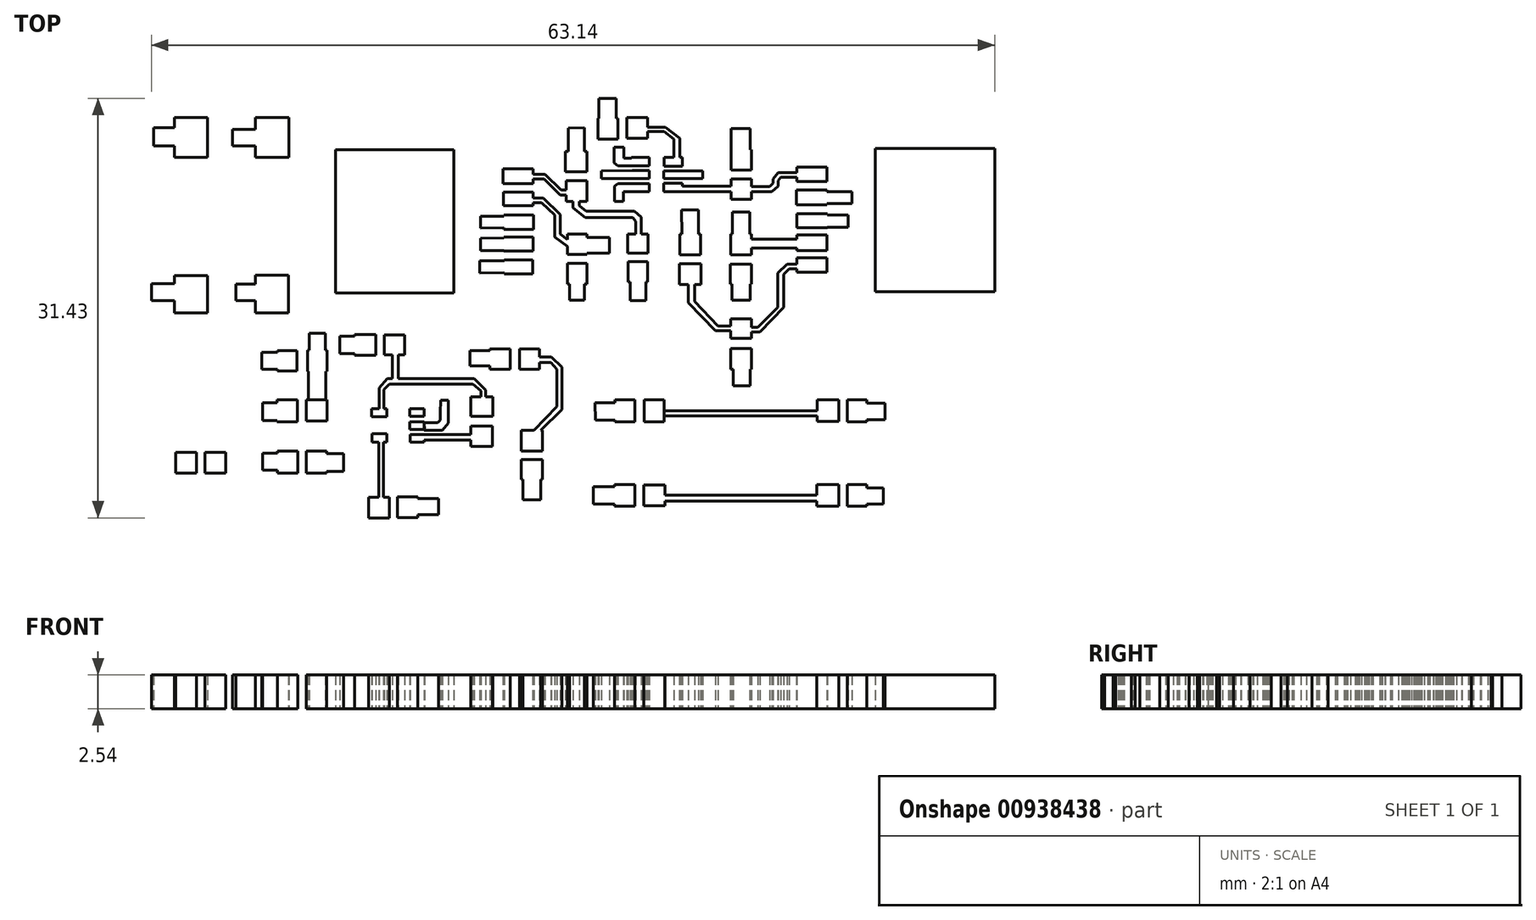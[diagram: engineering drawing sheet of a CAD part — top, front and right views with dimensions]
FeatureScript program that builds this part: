
annotation { "Feature Type Name" : "Feature", "Feature Type Description" : "" }
export const myFeature = defineFeature(function(context is Context, id is Id, definition is map)
    precondition{}
    {
        {
            var Q0;
            Q0=qCreatedBy(makeId("Top.planeOp"),FACE);
            var sketch = newSketch(context, id + "F0", { "sketchPlane" : qUnion([Q0])});
            skLineSegment(sketch, "E0.bottom", {"start": v(-32.78, 25.33) * mm, "end": v(35.8, 25.33) * mm});
            skLineSegment(sketch, "E0.top", {"start": v(-32.78, -28.01) * mm, "end": v(35.8, -28.01) * mm});
            skLineSegment(sketch, "E0.left", {"start": v(-32.78, 25.33) * mm, "end": v(-32.78, -28.01) * mm});
            skLineSegment(sketch, "E0.right", {"start": v(35.8, 25.33) * mm, "end": v(35.8, -28.01) * mm});
            skLineSegment(sketch, "E1.bottom", {"start": v(-28.35, 14.33) * mm, "end": v(-25.88, 14.33) * mm});
            skLineSegment(sketch, "E1.top", {"start": v(-28.35, 11.35) * mm, "end": v(-25.88, 11.35) * mm});
            skLineSegment(sketch, "E1.left", {"start": v(-28.35, 14.33) * mm, "end": v(-28.35, 11.35) * mm});
            skLineSegment(sketch, "E1.right", {"start": v(-25.88, 14.33) * mm, "end": v(-25.88, 11.35) * mm});
            skLineSegment(sketch, "E2.bottom", {"start": v(-22.29, 14.33) * mm, "end": v(-19.8, 14.33) * mm});
            skLineSegment(sketch, "E2.top", {"start": v(-22.29, 11.35) * mm, "end": v(-19.8, 11.35) * mm});
            skLineSegment(sketch, "E2.left", {"start": v(-22.29, 14.33) * mm, "end": v(-22.29, 11.35) * mm});
            skLineSegment(sketch, "E2.right", {"start": v(-19.8, 14.33) * mm, "end": v(-19.8, 11.35) * mm});
            skLineSegment(sketch, "E3.bottom", {"start": v(-28.35, 2.5) * mm, "end": v(-25.88, 2.5) * mm});
            skLineSegment(sketch, "E3.top", {"start": v(-28.35, -0.31) * mm, "end": v(-25.88, -0.31) * mm});
            skLineSegment(sketch, "E3.left", {"start": v(-28.35, 2.5) * mm, "end": v(-28.35, -0.31) * mm});
            skLineSegment(sketch, "E3.right", {"start": v(-25.88, 2.5) * mm, "end": v(-25.88, -0.31) * mm});
            skLineSegment(sketch, "E4.bottom", {"start": v(-22.29, 2.53) * mm, "end": v(-19.82, 2.53) * mm});
            skLineSegment(sketch, "E4.top", {"start": v(-22.29, -0.31) * mm, "end": v(-19.82, -0.31) * mm});
            skLineSegment(sketch, "E4.left", {"start": v(-22.29, 2.53) * mm, "end": v(-22.29, -0.31) * mm});
            skLineSegment(sketch, "E4.right", {"start": v(-19.82, 2.53) * mm, "end": v(-19.82, -0.31) * mm});
            skLineSegment(sketch, "E5.bottom", {"start": v(-28.24, -10.74) * mm, "end": v(-26.69, -10.74) * mm});
            skLineSegment(sketch, "E5.top", {"start": v(-28.24, -12.3) * mm, "end": v(-26.69, -12.3) * mm});
            skLineSegment(sketch, "E5.left", {"start": v(-28.24, -10.74) * mm, "end": v(-28.24, -12.3) * mm});
            skLineSegment(sketch, "E5.right", {"start": v(-26.69, -10.74) * mm, "end": v(-26.69, -12.3) * mm});
            skLineSegment(sketch, "E6.bottom", {"start": v(-26.08, -10.74) * mm, "end": v(-24.52, -10.74) * mm});
            skLineSegment(sketch, "E6.top", {"start": v(-26.08, -12.3) * mm, "end": v(-24.52, -12.3) * mm});
            skLineSegment(sketch, "E6.left", {"start": v(-26.08, -10.74) * mm, "end": v(-26.08, -12.3) * mm});
            skLineSegment(sketch, "E6.right", {"start": v(-24.52, -10.74) * mm, "end": v(-24.52, -12.3) * mm});
            skLineSegment(sketch, "E7.bottom", {"start": v(-20.64, -10.66) * mm, "end": v(-19.1, -10.66) * mm});
            skLineSegment(sketch, "E7.top", {"start": v(-20.64, -12.3) * mm, "end": v(-19.1, -12.3) * mm});
            skLineSegment(sketch, "E7.left", {"start": v(-20.64, -10.66) * mm, "end": v(-20.64, -12.3) * mm});
            skLineSegment(sketch, "E7.right", {"start": v(-19.1, -10.66) * mm, "end": v(-19.1, -12.3) * mm});
            skLineSegment(sketch, "E8.bottom", {"start": v(-18.47, -10.64) * mm, "end": v(-16.95, -10.64) * mm});
            skLineSegment(sketch, "E8.top", {"start": v(-18.47, -12.3) * mm, "end": v(-16.95, -12.3) * mm});
            skLineSegment(sketch, "E8.left", {"start": v(-18.47, -10.64) * mm, "end": v(-18.47, -12.3) * mm});
            skLineSegment(sketch, "E8.right", {"start": v(-16.95, -10.64) * mm, "end": v(-16.95, -12.3) * mm});
            skLineSegment(sketch, "E9.bottom", {"start": v(-20.66, -6.8) * mm, "end": v(-19.13, -6.8) * mm});
            skLineSegment(sketch, "E9.top", {"start": v(-20.66, -8.44) * mm, "end": v(-19.13, -8.44) * mm});
            skLineSegment(sketch, "E9.left", {"start": v(-20.66, -6.8) * mm, "end": v(-20.66, -8.44) * mm});
            skLineSegment(sketch, "E9.right", {"start": v(-19.13, -6.8) * mm, "end": v(-19.13, -8.44) * mm});
            skLineSegment(sketch, "E10.bottom", {"start": v(-18.47, -6.82) * mm, "end": v(-16.93, -6.82) * mm});
            skLineSegment(sketch, "E10.top", {"start": v(-18.47, -8.4) * mm, "end": v(-16.93, -8.4) * mm});
            skLineSegment(sketch, "E10.left", {"start": v(-18.47, -6.82) * mm, "end": v(-18.47, -8.4) * mm});
            skLineSegment(sketch, "E10.right", {"start": v(-16.93, -6.82) * mm, "end": v(-16.93, -8.4) * mm});
            skLineSegment(sketch, "E11.bottom", {"start": v(-20.64, -3.11) * mm, "end": v(-19.17, -3.11) * mm});
            skLineSegment(sketch, "E11.top", {"start": v(-20.64, -4.65) * mm, "end": v(-19.17, -4.65) * mm});
            skLineSegment(sketch, "E11.left", {"start": v(-20.64, -3.11) * mm, "end": v(-20.64, -4.65) * mm});
            skLineSegment(sketch, "E11.right", {"start": v(-19.17, -3.11) * mm, "end": v(-19.17, -4.65) * mm});
            skLineSegment(sketch, "E12.bottom", {"start": v(-18.38, -3.08) * mm, "end": v(-16.93, -3.08) * mm});
            skLineSegment(sketch, "E12.top", {"start": v(-18.38, -4.69) * mm, "end": v(-16.93, -4.69) * mm});
            skLineSegment(sketch, "E12.left", {"start": v(-18.38, -3.08) * mm, "end": v(-18.38, -4.69) * mm});
            skLineSegment(sketch, "E12.right", {"start": v(-16.93, -3.08) * mm, "end": v(-16.93, -4.69) * mm});
            skLineSegment(sketch, "E13.bottom", {"start": v(-14.86, -1.93) * mm, "end": v(-13.27, -1.93) * mm});
            skLineSegment(sketch, "E13.top", {"start": v(-14.86, -3.47) * mm, "end": v(-13.27, -3.47) * mm});
            skLineSegment(sketch, "E13.left", {"start": v(-14.86, -1.93) * mm, "end": v(-14.86, -3.47) * mm});
            skLineSegment(sketch, "E13.right", {"start": v(-13.27, -1.93) * mm, "end": v(-13.27, -3.47) * mm});
            skLineSegment(sketch, "E14.bottom", {"start": v(-12.63, -1.94) * mm, "end": v(-11.1, -1.94) * mm});
            skLineSegment(sketch, "E14.top", {"start": v(-12.63, -3.46) * mm, "end": v(-11.1, -3.46) * mm});
            skLineSegment(sketch, "E14.left", {"start": v(-12.63, -1.94) * mm, "end": v(-12.63, -3.46) * mm});
            skLineSegment(sketch, "E14.right", {"start": v(-11.1, -1.94) * mm, "end": v(-11.1, -3.46) * mm});
            skLineSegment(sketch, "E15.bottom", {"start": v(-13.59, -7.46) * mm, "end": v(-12.45, -7.46) * mm});
            skLineSegment(sketch, "E15.top", {"start": v(-13.59, -8.08) * mm, "end": v(-12.45, -8.08) * mm});
            skLineSegment(sketch, "E15.left", {"start": v(-13.59, -7.46) * mm, "end": v(-13.59, -8.08) * mm});
            skLineSegment(sketch, "E15.right", {"start": v(-12.45, -7.46) * mm, "end": v(-12.45, -8.08) * mm});
            skLineSegment(sketch, "E16.bottom", {"start": v(-10.74, -7.49) * mm, "end": v(-9.65, -7.49) * mm});
            skLineSegment(sketch, "E16.top", {"start": v(-10.74, -8.04) * mm, "end": v(-9.65, -8.04) * mm});
            skLineSegment(sketch, "E16.left", {"start": v(-10.74, -7.49) * mm, "end": v(-10.74, -8.04) * mm});
            skLineSegment(sketch, "E16.right", {"start": v(-9.65, -7.49) * mm, "end": v(-9.65, -8.04) * mm});
            skLineSegment(sketch, "E17.bottom", {"start": v(-10.74, -8.44) * mm, "end": v(-9.65, -8.44) * mm});
            skLineSegment(sketch, "E17.top", {"start": v(-10.74, -9.04) * mm, "end": v(-9.65, -9.04) * mm});
            skLineSegment(sketch, "E17.left", {"start": v(-10.74, -8.44) * mm, "end": v(-10.74, -9.04) * mm});
            skLineSegment(sketch, "E17.right", {"start": v(-9.65, -8.44) * mm, "end": v(-9.65, -9.04) * mm});
            skLineSegment(sketch, "E18.bottom", {"start": v(-10.69, -9.4) * mm, "end": v(-9.64, -9.4) * mm});
            skLineSegment(sketch, "E18.top", {"start": v(-10.69, -9.98) * mm, "end": v(-9.64, -9.98) * mm});
            skLineSegment(sketch, "E18.left", {"start": v(-10.69, -9.4) * mm, "end": v(-10.69, -9.98) * mm});
            skLineSegment(sketch, "E18.right", {"start": v(-9.64, -9.4) * mm, "end": v(-9.64, -9.98) * mm});
            skLineSegment(sketch, "E19.bottom", {"start": v(-13.56, -9.35) * mm, "end": v(-12.46, -9.35) * mm});
            skLineSegment(sketch, "E19.top", {"start": v(-13.56, -9.97) * mm, "end": v(-12.46, -9.97) * mm});
            skLineSegment(sketch, "E19.left", {"start": v(-13.56, -9.35) * mm, "end": v(-13.56, -9.97) * mm});
            skLineSegment(sketch, "E19.right", {"start": v(-12.46, -9.35) * mm, "end": v(-12.46, -9.97) * mm});
            skLineSegment(sketch, "E20.bottom", {"start": v(-6.15, -6.59) * mm, "end": v(-4.5, -6.59) * mm});
            skLineSegment(sketch, "E20.top", {"start": v(-6.15, -8.05) * mm, "end": v(-4.5, -8.05) * mm});
            skLineSegment(sketch, "E20.left", {"start": v(-6.15, -6.59) * mm, "end": v(-6.15, -8.05) * mm});
            skLineSegment(sketch, "E20.right", {"start": v(-4.5, -6.59) * mm, "end": v(-4.5, -8.05) * mm});
            skLineSegment(sketch, "E21.bottom", {"start": v(-6.15, -8.77) * mm, "end": v(-4.53, -8.77) * mm});
            skLineSegment(sketch, "E21.top", {"start": v(-6.15, -10.29) * mm, "end": v(-4.53, -10.29) * mm});
            skLineSegment(sketch, "E21.left", {"start": v(-6.15, -8.77) * mm, "end": v(-6.15, -10.29) * mm});
            skLineSegment(sketch, "E21.right", {"start": v(-4.53, -8.77) * mm, "end": v(-4.53, -10.29) * mm});
            skLineSegment(sketch, "E22.bottom", {"start": v(-13.82, -14.12) * mm, "end": v(-12.27, -14.12) * mm});
            skLineSegment(sketch, "E22.top", {"start": v(-13.82, -15.66) * mm, "end": v(-12.27, -15.66) * mm});
            skLineSegment(sketch, "E22.left", {"start": v(-13.82, -14.12) * mm, "end": v(-13.82, -15.66) * mm});
            skLineSegment(sketch, "E22.right", {"start": v(-12.27, -14.12) * mm, "end": v(-12.27, -15.66) * mm});
            skLineSegment(sketch, "E23.bottom", {"start": v(-11.64, -14.09) * mm, "end": v(-10.14, -14.09) * mm});
            skLineSegment(sketch, "E23.top", {"start": v(-11.64, -15.64) * mm, "end": v(-10.14, -15.64) * mm});
            skLineSegment(sketch, "E23.left", {"start": v(-11.64, -14.09) * mm, "end": v(-11.64, -15.64) * mm});
            skLineSegment(sketch, "E23.right", {"start": v(-10.14, -14.09) * mm, "end": v(-10.14, -15.64) * mm});
            skLineSegment(sketch, "E24.bottom", {"start": v(-2.38, -9.1) * mm, "end": v(-0.8, -9.1) * mm});
            skLineSegment(sketch, "E24.top", {"start": v(-2.38, -10.66) * mm, "end": v(-0.8, -10.66) * mm});
            skLineSegment(sketch, "E24.left", {"start": v(-2.38, -9.1) * mm, "end": v(-2.38, -10.66) * mm});
            skLineSegment(sketch, "E24.right", {"start": v(-0.8, -9.1) * mm, "end": v(-0.8, -10.66) * mm});
            skLineSegment(sketch, "E25.bottom", {"start": v(-2.4, -11.29) * mm, "end": v(-0.8, -11.29) * mm});
            skLineSegment(sketch, "E25.top", {"start": v(-2.4, -12.79) * mm, "end": v(-0.8, -12.79) * mm});
            skLineSegment(sketch, "E25.left", {"start": v(-2.4, -11.29) * mm, "end": v(-2.4, -12.79) * mm});
            skLineSegment(sketch, "E25.right", {"start": v(-0.8, -11.29) * mm, "end": v(-0.8, -12.79) * mm});
            skLineSegment(sketch, "E26.bottom", {"start": v(-4.75, -2.99) * mm, "end": v(-3.2, -2.99) * mm});
            skLineSegment(sketch, "E26.top", {"start": v(-4.75, -4.5) * mm, "end": v(-3.2, -4.5) * mm});
            skLineSegment(sketch, "E26.left", {"start": v(-4.75, -2.99) * mm, "end": v(-4.75, -4.5) * mm});
            skLineSegment(sketch, "E26.right", {"start": v(-3.2, -2.99) * mm, "end": v(-3.2, -4.5) * mm});
            skLineSegment(sketch, "E27.bottom", {"start": v(-2.5, -2.99) * mm, "end": v(-1.01, -2.99) * mm});
            skLineSegment(sketch, "E27.top", {"start": v(-2.5, -4.53) * mm, "end": v(-1.01, -4.53) * mm});
            skLineSegment(sketch, "E27.left", {"start": v(-2.5, -2.99) * mm, "end": v(-2.5, -4.53) * mm});
            skLineSegment(sketch, "E27.right", {"start": v(-1.01, -2.99) * mm, "end": v(-1.01, -4.53) * mm});
            skLineSegment(sketch, "E28.bottom", {"start": v(4.64, -6.82) * mm, "end": v(6.14, -6.82) * mm});
            skLineSegment(sketch, "E28.top", {"start": v(4.64, -8.45) * mm, "end": v(6.14, -8.45) * mm});
            skLineSegment(sketch, "E28.left", {"start": v(4.64, -6.82) * mm, "end": v(4.64, -8.45) * mm});
            skLineSegment(sketch, "E28.right", {"start": v(6.14, -6.82) * mm, "end": v(6.14, -8.45) * mm});
            skLineSegment(sketch, "E29.bottom", {"start": v(6.83, -6.82) * mm, "end": v(8.33, -6.82) * mm});
            skLineSegment(sketch, "E29.top", {"start": v(6.83, -8.46) * mm, "end": v(8.33, -8.46) * mm});
            skLineSegment(sketch, "E29.left", {"start": v(6.83, -6.82) * mm, "end": v(6.83, -8.46) * mm});
            skLineSegment(sketch, "E29.right", {"start": v(8.33, -6.82) * mm, "end": v(8.33, -8.46) * mm});
            skLineSegment(sketch, "E30.bottom", {"start": v(4.59, -13.14) * mm, "end": v(6.13, -13.14) * mm});
            skLineSegment(sketch, "E30.top", {"start": v(4.59, -14.79) * mm, "end": v(6.13, -14.79) * mm});
            skLineSegment(sketch, "E30.left", {"start": v(4.59, -13.14) * mm, "end": v(4.59, -14.79) * mm});
            skLineSegment(sketch, "E30.right", {"start": v(6.13, -13.14) * mm, "end": v(6.13, -14.79) * mm});
            skLineSegment(sketch, "E31.bottom", {"start": v(6.78, -13.18) * mm, "end": v(8.37, -13.18) * mm});
            skLineSegment(sketch, "E31.top", {"start": v(6.78, -14.75) * mm, "end": v(8.37, -14.75) * mm});
            skLineSegment(sketch, "E31.left", {"start": v(6.78, -13.18) * mm, "end": v(6.78, -14.75) * mm});
            skLineSegment(sketch, "E31.right", {"start": v(8.37, -13.18) * mm, "end": v(8.37, -14.75) * mm});
            skLineSegment(sketch, "E32.bottom", {"start": v(19.76, -13.17) * mm, "end": v(21.4, -13.17) * mm});
            skLineSegment(sketch, "E32.top", {"start": v(19.76, -14.77) * mm, "end": v(21.4, -14.77) * mm});
            skLineSegment(sketch, "E32.left", {"start": v(19.76, -13.17) * mm, "end": v(19.76, -14.77) * mm});
            skLineSegment(sketch, "E32.right", {"start": v(21.4, -13.17) * mm, "end": v(21.4, -14.77) * mm});
            skLineSegment(sketch, "E33.bottom", {"start": v(22.02, -13.15) * mm, "end": v(23.49, -13.15) * mm});
            skLineSegment(sketch, "E33.top", {"start": v(22.02, -14.77) * mm, "end": v(23.49, -14.77) * mm});
            skLineSegment(sketch, "E33.left", {"start": v(22.02, -13.15) * mm, "end": v(22.02, -14.77) * mm});
            skLineSegment(sketch, "E33.right", {"start": v(23.49, -13.15) * mm, "end": v(23.49, -14.77) * mm});
            skLineSegment(sketch, "E34.bottom", {"start": v(19.78, -6.82) * mm, "end": v(21.39, -6.82) * mm});
            skLineSegment(sketch, "E34.top", {"start": v(19.78, -8.44) * mm, "end": v(21.39, -8.44) * mm});
            skLineSegment(sketch, "E34.left", {"start": v(19.78, -6.82) * mm, "end": v(19.78, -8.44) * mm});
            skLineSegment(sketch, "E34.right", {"start": v(21.39, -6.82) * mm, "end": v(21.39, -8.44) * mm});
            skLineSegment(sketch, "E35.bottom", {"start": v(22.04, -6.82) * mm, "end": v(23.49, -6.82) * mm});
            skLineSegment(sketch, "E35.top", {"start": v(22.04, -8.47) * mm, "end": v(23.49, -8.47) * mm});
            skLineSegment(sketch, "E35.left", {"start": v(22.04, -6.82) * mm, "end": v(22.04, -8.47) * mm});
            skLineSegment(sketch, "E35.right", {"start": v(23.49, -6.82) * mm, "end": v(23.49, -8.47) * mm});
            skLineSegment(sketch, "E36.bottom", {"start": v(13.3, -0.74) * mm, "end": v(14.85, -0.74) * mm});
            skLineSegment(sketch, "E36.top", {"start": v(13.3, -2.22) * mm, "end": v(14.85, -2.22) * mm});
            skLineSegment(sketch, "E36.left", {"start": v(13.3, -0.74) * mm, "end": v(13.3, -2.22) * mm});
            skLineSegment(sketch, "E36.right", {"start": v(14.85, -0.74) * mm, "end": v(14.85, -2.22) * mm});
            skLineSegment(sketch, "E37.bottom", {"start": v(13.3, -2.96) * mm, "end": v(14.85, -2.96) * mm});
            skLineSegment(sketch, "E37.top", {"start": v(13.3, -4.53) * mm, "end": v(14.85, -4.53) * mm});
            skLineSegment(sketch, "E37.left", {"start": v(13.3, -2.96) * mm, "end": v(13.3, -4.53) * mm});
            skLineSegment(sketch, "E37.right", {"start": v(14.85, -2.96) * mm, "end": v(14.85, -4.53) * mm});
            skLineSegment(sketch, "E38.bottom", {"start": v(-16.28, 11.92) * mm, "end": v(-7.44, 11.92) * mm});
            skLineSegment(sketch, "E38.top", {"start": v(-16.28, 1.2) * mm, "end": v(-7.44, 1.2) * mm});
            skLineSegment(sketch, "E38.left", {"start": v(-16.28, 11.92) * mm, "end": v(-16.28, 1.2) * mm});
            skLineSegment(sketch, "E38.right", {"start": v(-7.44, 11.92) * mm, "end": v(-7.44, 1.2) * mm});
            skLineSegment(sketch, "E39.bottom", {"start": v(-3.76, 10.49) * mm, "end": v(-1.5, 10.49) * mm});
            skLineSegment(sketch, "E39.top", {"start": v(-3.76, 9.38) * mm, "end": v(-1.5, 9.38) * mm});
            skLineSegment(sketch, "E39.left", {"start": v(-3.76, 10.49) * mm, "end": v(-3.76, 9.38) * mm});
            skLineSegment(sketch, "E39.right", {"start": v(-1.5, 10.49) * mm, "end": v(-1.5, 9.38) * mm});
            skLineSegment(sketch, "E40.bottom", {"start": v(-3.7, 8.76) * mm, "end": v(-1.5, 8.76) * mm});
            skLineSegment(sketch, "E40.top", {"start": v(-3.7, 7.73) * mm, "end": v(-1.5, 7.73) * mm});
            skLineSegment(sketch, "E40.left", {"start": v(-3.7, 8.76) * mm, "end": v(-3.7, 7.73) * mm});
            skLineSegment(sketch, "E41.bottom", {"start": v(-3.67, 7.04) * mm, "end": v(-1.48, 7.04) * mm});
            skLineSegment(sketch, "E41.top", {"start": v(-3.67, 5.97) * mm, "end": v(-1.48, 5.97) * mm});
            skLineSegment(sketch, "E41.left", {"start": v(-3.67, 7.04) * mm, "end": v(-3.67, 5.97) * mm});
            skLineSegment(sketch, "E41.right", {"start": v(-1.48, 7.04) * mm, "end": v(-1.48, 5.97) * mm});
            skLineSegment(sketch, "E42.bottom", {"start": v(-3.67, 5.37) * mm, "end": v(-1.5, 5.37) * mm});
            skLineSegment(sketch, "E42.top", {"start": v(-3.67, 4.32) * mm, "end": v(-1.5, 4.32) * mm});
            skLineSegment(sketch, "E42.left", {"start": v(-3.67, 5.37) * mm, "end": v(-3.67, 4.32) * mm});
            skLineSegment(sketch, "E42.right", {"start": v(-1.5, 5.37) * mm, "end": v(-1.5, 4.32) * mm});
            skLineSegment(sketch, "E43.bottom", {"start": v(-3.66, 3.66) * mm, "end": v(-1.52, 3.66) * mm});
            skLineSegment(sketch, "E43.top", {"start": v(-3.66, 2.64) * mm, "end": v(-1.52, 2.64) * mm});
            skLineSegment(sketch, "E43.left", {"start": v(-3.66, 3.66) * mm, "end": v(-3.66, 2.64) * mm});
            skLineSegment(sketch, "E43.right", {"start": v(-1.52, 3.66) * mm, "end": v(-1.52, 2.64) * mm});
            skLineSegment(sketch, "E44.bottom", {"start": v(1.06, 5.6) * mm, "end": v(2.54, 5.6) * mm});
            skLineSegment(sketch, "E44.top", {"start": v(1.06, 4.1) * mm, "end": v(2.54, 4.1) * mm});
            skLineSegment(sketch, "E45.bottom", {"start": v(1.06, 3.4) * mm, "end": v(2.54, 3.4) * mm});
            skLineSegment(sketch, "E45.top", {"start": v(1.06, 1.85) * mm, "end": v(2.54, 1.85) * mm});
            skLineSegment(sketch, "E45.left", {"start": v(1.06, 3.4) * mm, "end": v(1.06, 1.85) * mm});
            skLineSegment(sketch, "E45.right", {"start": v(2.54, 3.4) * mm, "end": v(2.54, 1.85) * mm});
            skLineSegment(sketch, "E46.bottom", {"start": v(5.59, 5.6) * mm, "end": v(7.11, 5.6) * mm});
            skLineSegment(sketch, "E46.top", {"start": v(5.59, 4.2) * mm, "end": v(7.11, 4.2) * mm});
            skLineSegment(sketch, "E46.left", {"start": v(5.59, 5.6) * mm, "end": v(5.59, 4.2) * mm});
            skLineSegment(sketch, "E46.right", {"start": v(7.11, 5.6) * mm, "end": v(7.11, 4.2) * mm});
            skLineSegment(sketch, "E47.bottom", {"start": v(5.61, 3.54) * mm, "end": v(7.08, 3.54) * mm});
            skLineSegment(sketch, "E47.top", {"start": v(5.61, 2.01) * mm, "end": v(7.08, 2.01) * mm});
            skLineSegment(sketch, "E47.left", {"start": v(5.61, 3.54) * mm, "end": v(5.61, 2.01) * mm});
            skLineSegment(sketch, "E47.right", {"start": v(7.08, 3.54) * mm, "end": v(7.08, 2.01) * mm});
            skLineSegment(sketch, "E48.bottom", {"start": v(9.48, 5.6) * mm, "end": v(11.04, 5.6) * mm});
            skLineSegment(sketch, "E48.top", {"start": v(9.48, 4.05) * mm, "end": v(11.04, 4.05) * mm});
            skLineSegment(sketch, "E48.left", {"start": v(9.48, 5.6) * mm, "end": v(9.48, 4.05) * mm});
            skLineSegment(sketch, "E48.right", {"start": v(11.04, 5.6) * mm, "end": v(11.04, 4.05) * mm});
            skLineSegment(sketch, "E49.bottom", {"start": v(9.47, 3.38) * mm, "end": v(11.08, 3.38) * mm});
            skLineSegment(sketch, "E49.top", {"start": v(9.47, 1.84) * mm, "end": v(11.08, 1.84) * mm});
            skLineSegment(sketch, "E49.left", {"start": v(9.47, 3.38) * mm, "end": v(9.47, 1.84) * mm});
            skLineSegment(sketch, "E49.right", {"start": v(11.08, 3.38) * mm, "end": v(11.08, 1.84) * mm});
            skLineSegment(sketch, "E50.bottom", {"start": v(13.3, 5.6) * mm, "end": v(14.85, 5.6) * mm});
            skLineSegment(sketch, "E50.top", {"start": v(13.3, 4.05) * mm, "end": v(14.85, 4.05) * mm});
            skLineSegment(sketch, "E50.left", {"start": v(13.3, 5.6) * mm, "end": v(13.3, 4.05) * mm});
            skLineSegment(sketch, "E50.right", {"start": v(14.85, 5.6) * mm, "end": v(14.85, 4.05) * mm});
            skLineSegment(sketch, "E51.bottom", {"start": v(13.28, 3.36) * mm, "end": v(14.85, 3.36) * mm});
            skLineSegment(sketch, "E51.top", {"start": v(13.28, 1.87) * mm, "end": v(14.85, 1.87) * mm});
            skLineSegment(sketch, "E51.left", {"start": v(13.28, 3.36) * mm, "end": v(13.28, 1.87) * mm});
            skLineSegment(sketch, "E51.right", {"start": v(14.85, 3.36) * mm, "end": v(14.85, 1.87) * mm});
            skLineSegment(sketch, "E52.bottom", {"start": v(0.92, 11.8) * mm, "end": v(2.54, 11.8) * mm});
            skLineSegment(sketch, "E52.top", {"start": v(0.92, 10.26) * mm, "end": v(2.54, 10.26) * mm});
            skLineSegment(sketch, "E52.left", {"start": v(0.92, 11.8) * mm, "end": v(0.92, 10.26) * mm});
            skLineSegment(sketch, "E52.right", {"start": v(2.54, 11.8) * mm, "end": v(2.54, 10.26) * mm});
            skLineSegment(sketch, "E53.bottom", {"start": v(0.97, 9.62) * mm, "end": v(2.54, 9.62) * mm});
            skLineSegment(sketch, "E53.top", {"start": v(0.97, 8.05) * mm, "end": v(2.54, 8.05) * mm});
            skLineSegment(sketch, "E53.left", {"start": v(0.97, 9.62) * mm, "end": v(0.97, 8.05) * mm});
            skLineSegment(sketch, "E53.right", {"start": v(2.54, 9.62) * mm, "end": v(2.54, 8.05) * mm});
            skLineSegment(sketch, "E54.bottom", {"start": v(3.36, 14.27) * mm, "end": v(4.84, 14.27) * mm});
            skLineSegment(sketch, "E54.top", {"start": v(3.36, 12.73) * mm, "end": v(4.84, 12.73) * mm});
            skLineSegment(sketch, "E54.left", {"start": v(3.36, 14.27) * mm, "end": v(3.36, 12.73) * mm});
            skLineSegment(sketch, "E54.right", {"start": v(4.84, 14.27) * mm, "end": v(4.84, 12.73) * mm});
            skLineSegment(sketch, "E55.bottom", {"start": v(5.54, 14.33) * mm, "end": v(7.08, 14.33) * mm});
            skLineSegment(sketch, "E55.top", {"start": v(5.54, 12.77) * mm, "end": v(7.08, 12.77) * mm});
            skLineSegment(sketch, "E55.left", {"start": v(5.54, 14.33) * mm, "end": v(5.54, 12.77) * mm});
            skLineSegment(sketch, "E55.right", {"start": v(7.08, 14.33) * mm, "end": v(7.08, 12.77) * mm});
            skLineSegment(sketch, "E56.bottom", {"start": v(5.86, 11.35) * mm, "end": v(7.2, 11.35) * mm});
            skLineSegment(sketch, "E56.top", {"start": v(5.86, 10.72) * mm, "end": v(7.2, 10.72) * mm});
            skLineSegment(sketch, "E56.left", {"start": v(5.86, 11.35) * mm, "end": v(5.86, 10.72) * mm});
            skLineSegment(sketch, "E56.right", {"start": v(7.2, 11.35) * mm, "end": v(7.2, 10.72) * mm});
            skLineSegment(sketch, "E57.bottom", {"start": v(5.93, 10.35) * mm, "end": v(7.21, 10.35) * mm});
            skLineSegment(sketch, "E57.top", {"start": v(5.93, 9.76) * mm, "end": v(7.21, 9.76) * mm});
            skLineSegment(sketch, "E57.left", {"start": v(5.93, 10.35) * mm, "end": v(5.93, 9.76) * mm});
            skLineSegment(sketch, "E57.right", {"start": v(7.21, 10.35) * mm, "end": v(7.21, 9.76) * mm});
            skLineSegment(sketch, "E58.bottom", {"start": v(5.85, 9.4) * mm, "end": v(7.21, 9.4) * mm});
            skLineSegment(sketch, "E58.top", {"start": v(5.85, 8.78) * mm, "end": v(7.21, 8.78) * mm});
            skLineSegment(sketch, "E58.left", {"start": v(5.85, 9.4) * mm, "end": v(5.85, 8.78) * mm});
            skLineSegment(sketch, "E58.right", {"start": v(7.21, 9.4) * mm, "end": v(7.21, 8.78) * mm});
            skLineSegment(sketch, "E59.bottom", {"start": v(8.33, 11.35) * mm, "end": v(9.68, 11.35) * mm});
            skLineSegment(sketch, "E59.top", {"start": v(8.33, 10.67) * mm, "end": v(9.68, 10.67) * mm});
            skLineSegment(sketch, "E59.left", {"start": v(8.33, 11.35) * mm, "end": v(8.33, 10.67) * mm});
            skLineSegment(sketch, "E59.right", {"start": v(9.68, 11.35) * mm, "end": v(9.68, 10.67) * mm});
            skLineSegment(sketch, "E60.bottom", {"start": v(8.29, 10.34) * mm, "end": v(9.7, 10.34) * mm});
            skLineSegment(sketch, "E60.top", {"start": v(8.29, 9.77) * mm, "end": v(9.7, 9.77) * mm});
            skLineSegment(sketch, "E60.left", {"start": v(8.29, 10.34) * mm, "end": v(8.29, 9.77) * mm});
            skLineSegment(sketch, "E60.right", {"start": v(9.7, 10.34) * mm, "end": v(9.7, 9.77) * mm});
            skLineSegment(sketch, "E61.bottom", {"start": v(8.29, 9.42) * mm, "end": v(9.67, 9.42) * mm});
            skLineSegment(sketch, "E61.top", {"start": v(8.29, 8.78) * mm, "end": v(9.67, 8.78) * mm});
            skLineSegment(sketch, "E61.left", {"start": v(8.29, 9.42) * mm, "end": v(8.29, 8.78) * mm});
            skLineSegment(sketch, "E61.right", {"start": v(9.67, 9.42) * mm, "end": v(9.67, 8.78) * mm});
            skLineSegment(sketch, "E62.bottom", {"start": v(13.33, 11.94) * mm, "end": v(14.86, 11.94) * mm});
            skLineSegment(sketch, "E62.top", {"start": v(13.33, 10.4) * mm, "end": v(14.86, 10.4) * mm});
            skLineSegment(sketch, "E62.left", {"start": v(13.33, 11.94) * mm, "end": v(13.33, 10.4) * mm});
            skLineSegment(sketch, "E62.right", {"start": v(14.86, 11.94) * mm, "end": v(14.86, 10.4) * mm});
            skLineSegment(sketch, "E63.bottom", {"start": v(13.33, 9.73) * mm, "end": v(14.86, 9.73) * mm});
            skLineSegment(sketch, "E63.top", {"start": v(13.33, 8.2) * mm, "end": v(14.86, 8.2) * mm});
            skLineSegment(sketch, "E63.left", {"start": v(13.33, 9.73) * mm, "end": v(13.33, 8.2) * mm});
            skLineSegment(sketch, "E63.right", {"start": v(14.86, 9.73) * mm, "end": v(14.86, 8.2) * mm});
            skLineSegment(sketch, "E64.bottom", {"start": v(18.27, 10.62) * mm, "end": v(20.51, 10.62) * mm});
            skLineSegment(sketch, "E64.top", {"start": v(18.27, 9.55) * mm, "end": v(20.51, 9.55) * mm});
            skLineSegment(sketch, "E64.left", {"start": v(18.27, 10.62) * mm, "end": v(18.27, 9.55) * mm});
            skLineSegment(sketch, "E64.right", {"start": v(20.51, 10.62) * mm, "end": v(20.51, 9.55) * mm});
            skLineSegment(sketch, "E65.bottom", {"start": v(18.22, 8.91) * mm, "end": v(20.51, 8.91) * mm});
            skLineSegment(sketch, "E65.top", {"start": v(18.22, 7.81) * mm, "end": v(20.51, 7.81) * mm});
            skLineSegment(sketch, "E65.left", {"start": v(18.22, 8.91) * mm, "end": v(18.22, 7.81) * mm});
            skLineSegment(sketch, "E65.right", {"start": v(20.51, 8.91) * mm, "end": v(20.51, 7.81) * mm});
            skLineSegment(sketch, "E66.bottom", {"start": v(18.27, 7.13) * mm, "end": v(20.55, 7.13) * mm});
            skLineSegment(sketch, "E66.top", {"start": v(18.27, 6.07) * mm, "end": v(20.55, 6.07) * mm});
            skLineSegment(sketch, "E66.left", {"start": v(18.27, 7.13) * mm, "end": v(18.27, 6.07) * mm});
            skLineSegment(sketch, "E66.right", {"start": v(20.55, 7.13) * mm, "end": v(20.55, 6.07) * mm});
            skLineSegment(sketch, "E67.bottom", {"start": v(18.26, 5.56) * mm, "end": v(20.5, 5.56) * mm});
            skLineSegment(sketch, "E67.top", {"start": v(18.26, 4.38) * mm, "end": v(20.5, 4.38) * mm});
            skLineSegment(sketch, "E67.left", {"start": v(18.26, 5.56) * mm, "end": v(18.26, 4.38) * mm});
            skLineSegment(sketch, "E67.right", {"start": v(20.5, 5.56) * mm, "end": v(20.5, 4.38) * mm});
            skLineSegment(sketch, "E68.bottom", {"start": v(18.24, 3.83) * mm, "end": v(20.5, 3.83) * mm});
            skLineSegment(sketch, "E68.top", {"start": v(18.24, 2.76) * mm, "end": v(20.5, 2.76) * mm});
            skLineSegment(sketch, "E68.left", {"start": v(18.24, 3.83) * mm, "end": v(18.24, 2.76) * mm});
            skLineSegment(sketch, "E68.right", {"start": v(20.5, 3.83) * mm, "end": v(20.5, 2.76) * mm});
            skLineSegment(sketch, "E69.bottom", {"start": v(24.12, 12.03) * mm, "end": v(33.07, 12.03) * mm});
            skLineSegment(sketch, "E69.top", {"start": v(24.12, 1.3) * mm, "end": v(33.07, 1.3) * mm});
            skLineSegment(sketch, "E69.left", {"start": v(24.12, 12.03) * mm, "end": v(24.12, 1.3) * mm});
            skLineSegment(sketch, "E69.right", {"start": v(33.07, 12.03) * mm, "end": v(33.07, 1.3) * mm});
            skPoint(sketch, "E70.centerSnap0", {"position": v(-18.38, -3.89) * mm});
            skPoint(sketch, "E71.centerSnap0", {"position": v(-10.2, -7.49) * mm});
            skPoint(sketch, "E72.centerSnap0", {"position": v(14.06, 1.87) * mm});
            skLineSegment(sketch, "E73", {"start": v(-13.04, -14.12) * mm, "end": v(-13.04, -9.97) * mm});
            skLineSegment(sketch, "E74", {"start": v(-13.04, -9.97) * mm, "end": v(-12.7, -9.97) * mm});
            skLineSegment(sketch, "E75", {"start": v(-12.7, -9.97) * mm, "end": v(-12.7, -14.12) * mm});
            skLineSegment(sketch, "E76", {"start": v(-12.7, -14.12) * mm, "end": v(-13.04, -14.12) * mm});
            skLineSegment(sketch, "E77", {"start": v(-13.02, -7.46) * mm, "end": v(-13.02, -5.93) * mm});
            skLineSegment(sketch, "E78", {"start": v(-13.02, -5.93) * mm, "end": v(-12.43, -5.22) * mm});
            skLineSegment(sketch, "E79", {"start": v(-12.43, -5.22) * mm, "end": v(-12.05, -5.22) * mm});
            skLineSegment(sketch, "E80", {"start": v(-12.05, -5.22) * mm, "end": v(-12.05, -3.46) * mm});
            skLineSegment(sketch, "E81", {"start": v(-12.05, -3.46) * mm, "end": v(-11.6, -3.46) * mm});
            skLineSegment(sketch, "E82", {"start": v(-11.6, -3.46) * mm, "end": v(-11.6, -5.2) * mm});
            skLineSegment(sketch, "E83", {"start": v(-11.6, -5.2) * mm, "end": v(-5.9, -5.2) * mm});
            skLineSegment(sketch, "E84", {"start": v(-5.9, -5.2) * mm, "end": v(-5.05, -6.09) * mm});
            skLineSegment(sketch, "E85", {"start": v(-5.05, -6.09) * mm, "end": v(-5.05, -6.59) * mm});
            skLineSegment(sketch, "E86", {"start": v(-5.05, -6.59) * mm, "end": v(-5.33, -6.59) * mm});
            skLineSegment(sketch, "E87", {"start": v(-5.41, -6.59) * mm, "end": v(-5.41, -6.15) * mm});
            skLineSegment(sketch, "E88", {"start": v(-5.41, -6.15) * mm, "end": v(-6, -5.62) * mm});
            skLineSegment(sketch, "E89", {"start": v(-6, -5.62) * mm, "end": v(-12.26, -5.62) * mm});
            skLineSegment(sketch, "E90", {"start": v(-12.26, -5.62) * mm, "end": v(-12.66, -6.06) * mm});
            skLineSegment(sketch, "E91", {"start": v(-12.66, -6.06) * mm, "end": v(-12.66, -7.46) * mm});
            skLineSegment(sketch, "E92", {"start": v(-12.66, -7.46) * mm, "end": v(-13.02, -7.46) * mm});
            skLineSegment(sketch, "E93", {"start": v(-10.38, -7.49) * mm, "end": v(-9.77, -7.49) * mm});
            skLineSegment(sketch, "E94", {"start": v(-9.65, -8.54) * mm, "end": v(-8.64, -8.54) * mm});
            skLineSegment(sketch, "E95", {"start": v(-8.64, -8.54) * mm, "end": v(-8.44, -8.35) * mm});
            skLineSegment(sketch, "E96", {"start": v(-8.44, -8.35) * mm, "end": v(-8.44, -7.78) * mm});
            skLineSegment(sketch, "E97", {"start": v(-7.84, -7.78) * mm, "end": v(-7.84, -8.56) * mm});
            skLineSegment(sketch, "E98", {"start": v(-7.84, -8.56) * mm, "end": v(-8.3, -9.1) * mm});
            skLineSegment(sketch, "E99", {"start": v(-8.3, -9.1) * mm, "end": v(-9.65, -9.1) * mm});
            skLineSegment(sketch, "E100", {"start": v(-9.65, -9.1) * mm, "end": v(-9.64, -9.05) * mm});
            skLineSegment(sketch, "E101", {"start": v(-9.64, -9.05) * mm, "end": v(-9.65, -8.54) * mm});
            skLineSegment(sketch, "E102", {"start": v(-9.64, -9.4) * mm, "end": v(-6.15, -9.4) * mm});
            skLineSegment(sketch, "E103", {"start": v(-6.15, -9.4) * mm, "end": v(-6.15, -9.84) * mm});
            skLineSegment(sketch, "E104", {"start": v(-6.15, -9.84) * mm, "end": v(-9.64, -9.84) * mm});
            skLineSegment(sketch, "E105", {"start": v(-9.64, -9.84) * mm, "end": v(-9.64, -9.4) * mm});
            skLineSegment(sketch, "E106", {"start": v(-10.14, -15.5) * mm, "end": v(-10.14, -14.2) * mm});
            skLineSegment(sketch, "E107", {"start": v(-1.01, -4) * mm, "end": v(-0.17, -4) * mm});
            skLineSegment(sketch, "E108", {"start": v(-0.17, -4) * mm, "end": v(0.27, -4.52) * mm});
            skLineSegment(sketch, "E109", {"start": v(0.27, -4.52) * mm, "end": v(0.27, -7.32) * mm});
            skLineSegment(sketch, "E110", {"start": v(0.27, -7.32) * mm, "end": v(-1.41, -9.1) * mm});
            skLineSegment(sketch, "E111", {"start": v(-1.41, -9.1) * mm, "end": v(-0.8, -9.1) * mm});
            skLineSegment(sketch, "E112", {"start": v(-1.01, -3.6) * mm, "end": v(-0.13, -3.6) * mm});
            skLineSegment(sketch, "E113", {"start": v(-0.13, -3.6) * mm, "end": v(0.68, -4.36) * mm});
            skLineSegment(sketch, "E114", {"start": v(0.68, -4.36) * mm, "end": v(0.68, -7.54) * mm});
            skLineSegment(sketch, "E115", {"start": v(0.68, -7.54) * mm, "end": v(-0.94, -9.1) * mm});
            skLineSegment(sketch, "E116", {"start": v(-0.94, -9.1) * mm, "end": v(-1.41, -9.1) * mm});
            skLineSegment(sketch, "E117", {"start": v(8.33, -7.64) * mm, "end": v(19.78, -7.64) * mm});
            skLineSegment(sketch, "E118", {"start": v(19.78, -7.64) * mm, "end": v(19.78, -8.02) * mm});
            skLineSegment(sketch, "E119", {"start": v(19.78, -8.02) * mm, "end": v(8.33, -8.02) * mm});
            skLineSegment(sketch, "E120", {"start": v(8.33, -8.02) * mm, "end": v(8.33, -7.63) * mm});
            skLineSegment(sketch, "E121", {"start": v(8.37, -13.97) * mm, "end": v(19.76, -13.97) * mm});
            skLineSegment(sketch, "E122", {"start": v(19.76, -13.97) * mm, "end": v(19.76, -14.4) * mm});
            skLineSegment(sketch, "E123", {"start": v(19.76, -14.4) * mm, "end": v(8.33, -14.4) * mm});
            skLineSegment(sketch, "E124", {"start": v(8.33, -14.4) * mm, "end": v(8.37, -13.97) * mm});
            skLineSegment(sketch, "E125", {"start": v(-17.01, -4.69) * mm, "end": v(-17.01, -6.82) * mm});
            skLineSegment(sketch, "E126", {"start": v(-17.01, -6.82) * mm, "end": v(-18.34, -6.8) * mm});
            skLineSegment(sketch, "E127", {"start": v(-18.34, -6.8) * mm, "end": v(-18.34, -4.69) * mm});
            skLineSegment(sketch, "E128", {"start": v(-18.34, -4.69) * mm, "end": v(-17.01, -4.69) * mm});
            skLineSegment(sketch, "E129", {"start": v(10.14, 1.84) * mm, "end": v(10.14, 0.46) * mm});
            skLineSegment(sketch, "E130", {"start": v(10.14, 0.46) * mm, "end": v(12.17, -1.62) * mm});
            skLineSegment(sketch, "E131", {"start": v(12.17, -1.62) * mm, "end": v(13.3, -1.62) * mm});
            skLineSegment(sketch, "E132", {"start": v(13.3, -1.62) * mm, "end": v(13.3, -1.27) * mm});
            skLineSegment(sketch, "E133", {"start": v(13.3, -1.27) * mm, "end": v(12.35, -1.27) * mm});
            skLineSegment(sketch, "E134", {"start": v(12.35, -1.27) * mm, "end": v(10.59, 0.55) * mm});
            skLineSegment(sketch, "E135", {"start": v(10.59, 0.55) * mm, "end": v(10.59, 1.84) * mm});
            skLineSegment(sketch, "E136", {"start": v(10.59, 1.84) * mm, "end": v(10.14, 1.84) * mm});
            skLineSegment(sketch, "E137", {"start": v(14.85, -1.38) * mm, "end": v(15.34, -1.38) * mm});
            skLineSegment(sketch, "E138", {"start": v(15.34, -1.38) * mm, "end": v(16.83, 0.11) * mm});
            skLineSegment(sketch, "E139", {"start": v(16.83, 0.11) * mm, "end": v(16.83, 2.67) * mm});
            skLineSegment(sketch, "E140", {"start": v(16.83, 2.67) * mm, "end": v(17.53, 3.34) * mm});
            skLineSegment(sketch, "E141", {"start": v(17.53, 3.34) * mm, "end": v(18.24, 3.34) * mm});
            skLineSegment(sketch, "E142", {"start": v(18.24, 3.34) * mm, "end": v(18.24, 3) * mm});
            skLineSegment(sketch, "E143", {"start": v(18.24, 3) * mm, "end": v(17.67, 3) * mm});
            skLineSegment(sketch, "E144", {"start": v(17.67, 3) * mm, "end": v(17.26, 2.6) * mm});
            skLineSegment(sketch, "E145", {"start": v(17.26, 2.6) * mm, "end": v(17.26, 0.1) * mm});
            skLineSegment(sketch, "E146", {"start": v(17.26, 0.1) * mm, "end": v(15.5, -1.73) * mm});
            skLineSegment(sketch, "E147", {"start": v(15.5, -1.73) * mm, "end": v(14.85, -1.73) * mm});
            skLineSegment(sketch, "E148", {"start": v(14.85, -1.73) * mm, "end": v(14.85, -1.38) * mm});
            skLineSegment(sketch, "E149", {"start": v(14.85, 4.56) * mm, "end": v(18.26, 4.56) * mm});
            skLineSegment(sketch, "E150", {"start": v(18.26, 4.56) * mm, "end": v(18.26, 5.23) * mm});
            skLineSegment(sketch, "E151", {"start": v(18.26, 5.23) * mm, "end": v(14.85, 5.23) * mm});
            skLineSegment(sketch, "E152", {"start": v(14.85, 5.23) * mm, "end": v(14.85, 4.56) * mm});
            skLineSegment(sketch, "E153", {"start": v(6.6, 5.6) * mm, "end": v(6.6, 6.87) * mm});
            skLineSegment(sketch, "E154", {"start": v(6.6, 6.87) * mm, "end": v(6.1, 7.3) * mm});
            skLineSegment(sketch, "E155", {"start": v(6.1, 7.3) * mm, "end": v(2.48, 7.3) * mm});
            skLineSegment(sketch, "E156", {"start": v(2.48, 7.3) * mm, "end": v(1.97, 7.73) * mm});
            skLineSegment(sketch, "E157", {"start": v(1.97, 7.73) * mm, "end": v(1.97, 8.05) * mm});
            skLineSegment(sketch, "E158", {"start": v(1.97, 8.05) * mm, "end": v(1.48, 8.05) * mm});
            skLineSegment(sketch, "E159", {"start": v(1.48, 8.05) * mm, "end": v(1.48, 7.58) * mm});
            skLineSegment(sketch, "E160", {"start": v(1.48, 7.58) * mm, "end": v(2.4, 6.84) * mm});
            skLineSegment(sketch, "E161", {"start": v(2.4, 6.84) * mm, "end": v(5.97, 6.84) * mm});
            skLineSegment(sketch, "E162", {"start": v(5.97, 6.84) * mm, "end": v(6.2, 6.57) * mm});
            skLineSegment(sketch, "E163", {"start": v(6.2, 6.57) * mm, "end": v(6.2, 5.6) * mm});
            skLineSegment(sketch, "E164", {"start": v(6.2, 5.6) * mm, "end": v(6.6, 5.6) * mm});
            skLineSegment(sketch, "E165", {"start": v(1.06, 5.19) * mm, "end": v(0.53, 5.6) * mm});
            skLineSegment(sketch, "E166", {"start": v(0.53, 5.6) * mm, "end": v(0.53, 7.08) * mm});
            skLineSegment(sketch, "E167", {"start": v(0.53, 7.08) * mm, "end": v(-0.72, 8.32) * mm});
            skLineSegment(sketch, "E168", {"start": v(-0.72, 8.32) * mm, "end": v(-1.5, 8.32) * mm});
            skLineSegment(sketch, "E169", {"start": v(-1.5, 7.97) * mm, "end": v(-0.87, 7.97) * mm});
            skLineSegment(sketch, "E170", {"start": v(0.97, 8.52) * mm, "end": v(0.53, 8.52) * mm});
            skLineSegment(sketch, "E171", {"start": v(0.53, 8.52) * mm, "end": v(-0.68, 9.72) * mm});
            skLineSegment(sketch, "E172", {"start": v(-0.68, 9.72) * mm, "end": v(-1.5, 9.72) * mm});
            skLineSegment(sketch, "E173", {"start": v(-1.5, 9.72) * mm, "end": v(-1.5, 10.1) * mm});
            skLineSegment(sketch, "E174", {"start": v(-1.5, 10.1) * mm, "end": v(-0.62, 10.1) * mm});
            skLineSegment(sketch, "E175", {"start": v(-0.62, 10.1) * mm, "end": v(0.6, 8.9) * mm});
            skLineSegment(sketch, "E176", {"start": v(0.6, 8.9) * mm, "end": v(0.97, 8.9) * mm});
            skLineSegment(sketch, "E177", {"start": v(0.97, 8.9) * mm, "end": v(0.97, 8.52) * mm});
            skLineSegment(sketch, "E178", {"start": v(7.08, 13.28) * mm, "end": v(8.32, 13.28) * mm});
            skLineSegment(sketch, "E179", {"start": v(8.32, 13.28) * mm, "end": v(9.05, 12.7) * mm});
            skLineSegment(sketch, "E180", {"start": v(9.05, 12.7) * mm, "end": v(9.05, 11.35) * mm});
            skLineSegment(sketch, "E181", {"start": v(9.05, 11.35) * mm, "end": v(9.48, 11.35) * mm});
            skLineSegment(sketch, "E182", {"start": v(9.48, 11.35) * mm, "end": v(9.48, 12.78) * mm});
            skLineSegment(sketch, "E183", {"start": v(9.48, 12.78) * mm, "end": v(8.42, 13.62) * mm});
            skLineSegment(sketch, "E184", {"start": v(8.42, 13.62) * mm, "end": v(7.08, 13.62) * mm});
            skLineSegment(sketch, "E185", {"start": v(7.08, 13.62) * mm, "end": v(7.08, 13.28) * mm});
            skLineSegment(sketch, "E186", {"start": v(9.67, 8.78) * mm, "end": v(13.33, 8.78) * mm});
            skLineSegment(sketch, "E187", {"start": v(13.33, 8.78) * mm, "end": v(13.33, 9.2) * mm});
            skLineSegment(sketch, "E188", {"start": v(13.33, 9.2) * mm, "end": v(9.67, 9.2) * mm});
            skLineSegment(sketch, "E189", {"start": v(9.67, 9.2) * mm, "end": v(9.67, 8.78) * mm});
            skLineSegment(sketch, "E190", {"start": v(14.86, 8.78) * mm, "end": v(16.38, 8.78) * mm});
            skLineSegment(sketch, "E191", {"start": v(16.38, 8.78) * mm, "end": v(16.85, 9.2) * mm});
            skLineSegment(sketch, "E192", {"start": v(16.85, 9.2) * mm, "end": v(16.85, 9.61) * mm});
            skLineSegment(sketch, "E193", {"start": v(16.85, 9.61) * mm, "end": v(17.05, 9.86) * mm});
            skLineSegment(sketch, "E194", {"start": v(17.05, 9.86) * mm, "end": v(18.26, 9.87) * mm});
            skLineSegment(sketch, "E195", {"start": v(18.26, 9.87) * mm, "end": v(18.27, 10.22) * mm});
            skLineSegment(sketch, "E196", {"start": v(14.86, 9.17) * mm, "end": v(14.86, 8.78) * mm});
            skLineSegment(sketch, "E197", {"start": v(18.27, 10.22) * mm, "end": v(16.86, 10.22) * mm});
            skLineSegment(sketch, "E198", {"start": v(16.86, 10.22) * mm, "end": v(16.49, 9.73) * mm});
            skLineSegment(sketch, "E199", {"start": v(16.49, 9.73) * mm, "end": v(16.49, 9.41) * mm});
            skLineSegment(sketch, "E200", {"start": v(16.49, 9.41) * mm, "end": v(16.23, 9.17) * mm});
            skLineSegment(sketch, "E201", {"start": v(16.23, 9.17) * mm, "end": v(14.86, 9.17) * mm});
            skLineSegment(sketch, "E202", {"start": v(-24.52, -10.87) * mm, "end": v(-24.52, -12.17) * mm});
            skLineSegment(sketch, "E203", {"start": v(-28.24, -10.87) * mm, "end": v(-28.24, -12.17) * mm});
            skLineSegment(sketch, "E204", {"start": v(-22.29, 0.61) * mm, "end": v(-23.76, 0.61) * mm});
            skLineSegment(sketch, "E205", {"start": v(-23.76, 0.61) * mm, "end": v(-23.76, 1.87) * mm});
            skLineSegment(sketch, "E206", {"start": v(-23.76, 1.87) * mm, "end": v(-22.29, 1.87) * mm});
            skLineSegment(sketch, "E207", {"start": v(-22.29, 1.87) * mm, "end": v(-22.29, 0.61) * mm});
            skLineSegment(sketch, "E208", {"start": v(-28.35, 0.61) * mm, "end": v(-30.07, 0.61) * mm});
            skLineSegment(sketch, "E209", {"start": v(-30.07, 0.61) * mm, "end": v(-30.07, 1.9) * mm});
            skLineSegment(sketch, "E210", {"start": v(-30.07, 1.9) * mm, "end": v(-28.35, 1.9) * mm});
            skLineSegment(sketch, "E211", {"start": v(-28.35, 1.9) * mm, "end": v(-28.35, 0.61) * mm});
            skLineSegment(sketch, "E212", {"start": v(-20.64, -3.24) * mm, "end": v(-21.81, -3.24) * mm});
            skLineSegment(sketch, "E213", {"start": v(-21.81, -3.24) * mm, "end": v(-21.81, -4.53) * mm});
            skLineSegment(sketch, "E214", {"start": v(-21.81, -4.53) * mm, "end": v(-20.64, -4.53) * mm});
            skLineSegment(sketch, "E215", {"start": v(-20.64, -4.53) * mm, "end": v(-20.64, -3.24) * mm});
            skLineSegment(sketch, "E216", {"start": v(-20.66, -8.36) * mm, "end": v(-21.75, -8.36) * mm});
            skLineSegment(sketch, "E217", {"start": v(-21.75, -8.36) * mm, "end": v(-21.75, -7.04) * mm});
            skLineSegment(sketch, "E218", {"start": v(-21.75, -7.04) * mm, "end": v(-20.66, -7.04) * mm});
            skLineSegment(sketch, "E219", {"start": v(-20.66, -7.04) * mm, "end": v(-20.66, -8.36) * mm});
            skLineSegment(sketch, "E220", {"start": v(-20.66, -8.3) * mm, "end": v(-20.66, -8.36) * mm});
            skLineSegment(sketch, "E221", {"start": v(-24.52, -10.87) * mm, "end": v(-23.29, -10.87) * mm});
            skLineSegment(sketch, "E222", {"start": v(-23.29, -10.87) * mm, "end": v(-23.29, -12.17) * mm});
            skLineSegment(sketch, "E223", {"start": v(-23.29, -12.17) * mm, "end": v(-24.52, -12.17) * mm});
            skLineSegment(sketch, "E224", {"start": v(-28.24, -10.87) * mm, "end": v(-29.68, -10.87) * mm});
            skLineSegment(sketch, "E225", {"start": v(-29.68, -10.87) * mm, "end": v(-29.68, -12.16) * mm});
            skLineSegment(sketch, "E226", {"start": v(-29.68, -12.16) * mm, "end": v(-28.24, -12.17) * mm});
            skLineSegment(sketch, "E227", {"start": v(-20.64, -10.8) * mm, "end": v(-21.77, -10.8) * mm});
            skLineSegment(sketch, "E228", {"start": v(-21.77, -10.8) * mm, "end": v(-21.77, -12.07) * mm});
            skLineSegment(sketch, "E229", {"start": v(-21.77, -12.07) * mm, "end": v(-20.64, -12.07) * mm});
            skLineSegment(sketch, "E230", {"start": v(-16.95, -10.84) * mm, "end": v(-15.67, -10.84) * mm});
            skLineSegment(sketch, "E231", {"start": v(-15.67, -10.84) * mm, "end": v(-15.67, -12.17) * mm});
            skLineSegment(sketch, "E232", {"start": v(-15.67, -12.17) * mm, "end": v(-16.95, -12.17) * mm});
            skLineSegment(sketch, "E233", {"start": v(-16.95, -12.17) * mm, "end": v(-16.95, -10.84) * mm});
            skLineSegment(sketch, "E234", {"start": v(-7.84, -7.78) * mm, "end": v(-7.84, -6.84) * mm});
            skLineSegment(sketch, "E235", {"start": v(-7.84, -6.84) * mm, "end": v(-8.4, -6.84) * mm});
            skLineSegment(sketch, "E236", {"start": v(-8.4, -6.84) * mm, "end": v(-8.44, -7.78) * mm});
            skLineSegment(sketch, "E237", {"start": v(-9.77, -7.49) * mm, "end": v(-9.77, -6.06) * mm});
            skLineSegment(sketch, "E238", {"start": v(-9.77, -6.06) * mm, "end": v(-10.58, -6.06) * mm});
            skLineSegment(sketch, "E239", {"start": v(-10.58, -6.06) * mm, "end": v(-10.58, -7) * mm});
            skLineSegment(sketch, "E240", {"start": v(-10.58, -7) * mm, "end": v(-10.4, -7) * mm});
            skLineSegment(sketch, "E241", {"start": v(-10.4, -7) * mm, "end": v(-10.38, -7.49) * mm});
            skLineSegment(sketch, "E242", {"start": v(-17.07, -3.08) * mm, "end": v(-17.07, -1.81) * mm});
            skLineSegment(sketch, "E243", {"start": v(-17.07, -1.81) * mm, "end": v(-18.27, -1.81) * mm});
            skLineSegment(sketch, "E244", {"start": v(-18.27, -1.81) * mm, "end": v(-18.27, -3.08) * mm});
            skLineSegment(sketch, "E245", {"start": v(-18.27, -3.08) * mm, "end": v(-17.04, -3.09) * mm});
            skLineSegment(sketch, "E246", {"start": v(-14.86, -3.34) * mm, "end": v(-15.97, -3.34) * mm});
            skLineSegment(sketch, "E247", {"start": v(-15.97, -3.34) * mm, "end": v(-15.97, -2.03) * mm});
            skLineSegment(sketch, "E248", {"start": v(-15.97, -2.03) * mm, "end": v(-14.86, -2.03) * mm});
            skLineSegment(sketch, "E249", {"start": v(-14.86, -2.03) * mm, "end": v(-14.86, -3.34) * mm});
            skLineSegment(sketch, "E250", {"start": v(-10.14, -14.2) * mm, "end": v(-8.58, -14.2) * mm});
            skLineSegment(sketch, "E251", {"start": v(-8.58, -14.2) * mm, "end": v(-8.58, -15.42) * mm});
            skLineSegment(sketch, "E252", {"start": v(-8.58, -15.42) * mm, "end": v(-10.14, -15.42) * mm});
            skLineSegment(sketch, "E253", {"start": v(-10.14, -15.42) * mm, "end": v(-10.14, -14.2) * mm});
            skLineSegment(sketch, "E254", {"start": v(-4.75, -4.28) * mm, "end": v(-6.24, -4.28) * mm});
            skLineSegment(sketch, "E255", {"start": v(-6.24, -4.28) * mm, "end": v(-6.24, -3.11) * mm});
            skLineSegment(sketch, "E256", {"start": v(-6.24, -3.11) * mm, "end": v(-4.75, -3.11) * mm});
            skLineSegment(sketch, "E257", {"start": v(-4.75, -3.11) * mm, "end": v(-4.75, -4.28) * mm});
            skLineSegment(sketch, "E258", {"start": v(-0.94, -12.79) * mm, "end": v(-0.94, -14.3) * mm});
            skLineSegment(sketch, "E259", {"start": v(-0.94, -14.3) * mm, "end": v(-2.24, -14.3) * mm});
            skLineSegment(sketch, "E260", {"start": v(-2.24, -14.3) * mm, "end": v(-2.24, -12.79) * mm});
            skLineSegment(sketch, "E261", {"start": v(-2.24, -12.79) * mm, "end": v(-0.94, -12.79) * mm});
            skLineSegment(sketch, "E262", {"start": v(4.59, -14.61) * mm, "end": v(3.02, -14.61) * mm});
            skLineSegment(sketch, "E263", {"start": v(3.02, -14.61) * mm, "end": v(3.02, -13.32) * mm});
            skLineSegment(sketch, "E264", {"start": v(3.02, -13.32) * mm, "end": v(4.59, -13.32) * mm});
            skLineSegment(sketch, "E265", {"start": v(4.59, -13.32) * mm, "end": v(4.59, -14.61) * mm});
            skLineSegment(sketch, "E266", {"start": v(23.49, -14.61) * mm, "end": v(24.74, -14.61) * mm});
            skLineSegment(sketch, "E267", {"start": v(24.74, -14.61) * mm, "end": v(24.74, -13.42) * mm});
            skLineSegment(sketch, "E268", {"start": v(24.74, -13.42) * mm, "end": v(23.49, -13.42) * mm});
            skLineSegment(sketch, "E269", {"start": v(23.49, -13.42) * mm, "end": v(23.49, -14.61) * mm});
            skLineSegment(sketch, "E270", {"start": v(23.49, -8.3) * mm, "end": v(24.87, -8.3) * mm});
            skLineSegment(sketch, "E271", {"start": v(24.87, -8.3) * mm, "end": v(24.87, -7.05) * mm});
            skLineSegment(sketch, "E272", {"start": v(24.87, -7.05) * mm, "end": v(23.49, -7.05) * mm});
            skLineSegment(sketch, "E273", {"start": v(23.49, -7.05) * mm, "end": v(23.49, -8.3) * mm});
            skLineSegment(sketch, "E274", {"start": v(14.75, -4.53) * mm, "end": v(14.75, -5.76) * mm});
            skLineSegment(sketch, "E275", {"start": v(14.75, -5.76) * mm, "end": v(13.48, -5.76) * mm});
            skLineSegment(sketch, "E276", {"start": v(13.48, -5.76) * mm, "end": v(13.48, -4.53) * mm});
            skLineSegment(sketch, "E277", {"start": v(13.48, -4.53) * mm, "end": v(14.75, -4.53) * mm});
            skLineSegment(sketch, "E278", {"start": v(6.94, 2.01) * mm, "end": v(6.94, 0.61) * mm});
            skLineSegment(sketch, "E279", {"start": v(6.94, 0.61) * mm, "end": v(5.8, 0.61) * mm});
            skLineSegment(sketch, "E280", {"start": v(5.8, 0.61) * mm, "end": v(5.8, 2.01) * mm});
            skLineSegment(sketch, "E281", {"start": v(5.8, 2.01) * mm, "end": v(6.94, 2.01) * mm});
            skLineSegment(sketch, "E282", {"start": v(2.36, 1.85) * mm, "end": v(2.36, 0.66) * mm});
            skLineSegment(sketch, "E283", {"start": v(2.36, 0.66) * mm, "end": v(1.23, 0.66) * mm});
            skLineSegment(sketch, "E284", {"start": v(1.23, 0.66) * mm, "end": v(1.23, 1.85) * mm});
            skLineSegment(sketch, "E285", {"start": v(1.23, 1.85) * mm, "end": v(2.36, 1.85) * mm});
            skLineSegment(sketch, "E286", {"start": v(2.54, 4.2) * mm, "end": v(4.2, 4.2) * mm});
            skLineSegment(sketch, "E287", {"start": v(4.2, 4.2) * mm, "end": v(4.2, 5.36) * mm});
            skLineSegment(sketch, "E288", {"start": v(4.2, 5.36) * mm, "end": v(2.54, 5.36) * mm});
            skLineSegment(sketch, "E289", {"start": v(5.85, 9.4) * mm, "end": v(4.84, 9.4) * mm});
            skLineSegment(sketch, "E290", {"start": v(4.84, 9.4) * mm, "end": v(4.59, 9.2) * mm});
            skLineSegment(sketch, "E291", {"start": v(4.59, 9.2) * mm, "end": v(4.59, 8.07) * mm});
            skLineSegment(sketch, "E292", {"start": v(4.59, 8.07) * mm, "end": v(5.27, 8.07) * mm});
            skLineSegment(sketch, "E293", {"start": v(5.27, 8.07) * mm, "end": v(5.27, 8.79) * mm});
            skLineSegment(sketch, "E294", {"start": v(5.27, 8.79) * mm, "end": v(5.85, 8.78) * mm});
            skLineSegment(sketch, "E295", {"start": v(5.93, 9.76) * mm, "end": v(3.61, 9.76) * mm});
            skLineSegment(sketch, "E296", {"start": v(3.61, 9.76) * mm, "end": v(3.61, 10.35) * mm});
            skLineSegment(sketch, "E297", {"start": v(3.61, 10.35) * mm, "end": v(5.93, 10.35) * mm});
            skLineSegment(sketch, "E298", {"start": v(9.7, 10.34) * mm, "end": v(11.21, 10.34) * mm});
            skLineSegment(sketch, "E299", {"start": v(11.21, 10.34) * mm, "end": v(11.21, 9.76) * mm});
            skLineSegment(sketch, "E300", {"start": v(11.21, 9.76) * mm, "end": v(9.7, 9.77) * mm});
            skLineSegment(sketch, "E301", {"start": v(5.86, 10.72) * mm, "end": v(4.84, 10.72) * mm});
            skLineSegment(sketch, "E302", {"start": v(4.84, 10.72) * mm, "end": v(4.58, 10.94) * mm});
            skLineSegment(sketch, "E303", {"start": v(4.58, 10.94) * mm, "end": v(4.57, 12.12) * mm});
            skLineSegment(sketch, "E304", {"start": v(4.57, 12.12) * mm, "end": v(5.3, 12.12) * mm});
            skLineSegment(sketch, "E305", {"start": v(5.3, 12.12) * mm, "end": v(5.3, 11.3) * mm});
            skLineSegment(sketch, "E306", {"start": v(5.3, 11.3) * mm, "end": v(5.86, 11.3) * mm});
            skLineSegment(sketch, "E307", {"start": v(5.86, 11.3) * mm, "end": v(5.86, 10.72) * mm});
            skLineSegment(sketch, "E308", {"start": v(2.34, 11.8) * mm, "end": v(2.34, 13.56) * mm});
            skLineSegment(sketch, "E309", {"start": v(2.34, 13.56) * mm, "end": v(1.13, 13.56) * mm});
            skLineSegment(sketch, "E310", {"start": v(1.13, 13.56) * mm, "end": v(1.14, 11.8) * mm});
            skLineSegment(sketch, "E311", {"start": v(1.14, 11.8) * mm, "end": v(2.34, 11.8) * mm});
            skLineSegment(sketch, "E312", {"start": v(14.77, 11.94) * mm, "end": v(14.76, 13.53) * mm});
            skLineSegment(sketch, "E313", {"start": v(14.76, 13.53) * mm, "end": v(13.33, 13.52) * mm});
            skLineSegment(sketch, "E314", {"start": v(13.33, 13.52) * mm, "end": v(13.33, 11.94) * mm});
            skLineSegment(sketch, "E315", {"start": v(9.64, 5.6) * mm, "end": v(9.63, 7.4) * mm});
            skLineSegment(sketch, "E316", {"start": v(9.63, 7.4) * mm, "end": v(10.88, 7.4) * mm});
            skLineSegment(sketch, "E317", {"start": v(10.88, 7.4) * mm, "end": v(10.89, 5.6) * mm});
            skLineSegment(sketch, "E318", {"start": v(10.89, 5.6) * mm, "end": v(9.64, 5.6) * mm});
            skLineSegment(sketch, "E319", {"start": v(13.42, 5.6) * mm, "end": v(13.42, 7.25) * mm});
            skLineSegment(sketch, "E320", {"start": v(13.42, 7.25) * mm, "end": v(14.73, 7.25) * mm});
            skLineSegment(sketch, "E321", {"start": v(14.73, 7.25) * mm, "end": v(14.73, 5.6) * mm});
            skLineSegment(sketch, "E322", {"start": v(14.73, 5.6) * mm, "end": v(13.42, 5.6) * mm});
            skLineSegment(sketch, "E323", {"start": v(20.51, 7.9) * mm, "end": v(22.37, 7.9) * mm});
            skLineSegment(sketch, "E324", {"start": v(22.37, 7.9) * mm, "end": v(22.37, 8.8) * mm});
            skLineSegment(sketch, "E325", {"start": v(22.37, 8.8) * mm, "end": v(20.51, 8.8) * mm});
            skLineSegment(sketch, "E326", {"start": v(20.51, 8.8) * mm, "end": v(20.51, 7.9) * mm});
            skLineSegment(sketch, "E327", {"start": v(20.55, 7.04) * mm, "end": v(22.1, 7.04) * mm});
            skLineSegment(sketch, "E328", {"start": v(22.1, 7.04) * mm, "end": v(22.1, 6.11) * mm});
            skLineSegment(sketch, "E329", {"start": v(22.1, 6.11) * mm, "end": v(20.55, 6.11) * mm});
            skLineSegment(sketch, "E330", {"start": v(20.55, 6.11) * mm, "end": v(20.55, 7.04) * mm});
            skLineSegment(sketch, "E331", {"start": v(14.75, 1.87) * mm, "end": v(14.75, 0.65) * mm});
            skLineSegment(sketch, "E332", {"start": v(14.75, 0.65) * mm, "end": v(13.39, 0.65) * mm});
            skLineSegment(sketch, "E333", {"start": v(13.39, 0.65) * mm, "end": v(13.39, 1.87) * mm});
            skLineSegment(sketch, "E334", {"start": v(13.39, 1.87) * mm, "end": v(14.75, 1.87) * mm});
            skLineSegment(sketch, "E335", {"start": v(-22.29, 12.2) * mm, "end": v(-24, 12.2) * mm});
            skLineSegment(sketch, "E336", {"start": v(-24, 12.2) * mm, "end": v(-24, 13.45) * mm});
            skLineSegment(sketch, "E337", {"start": v(-24, 13.45) * mm, "end": v(-22.29, 13.45) * mm});
            skLineSegment(sketch, "E338", {"start": v(-22.29, 13.45) * mm, "end": v(-22.29, 12.2) * mm});
            skLineSegment(sketch, "E339", {"start": v(-28.35, 12.2) * mm, "end": v(-29.92, 12.2) * mm});
            skLineSegment(sketch, "E340", {"start": v(-29.92, 12.2) * mm, "end": v(-29.92, 13.59) * mm});
            skLineSegment(sketch, "E341", {"start": v(-29.92, 13.59) * mm, "end": v(-28.35, 13.59) * mm});
            skLineSegment(sketch, "E342", {"start": v(-28.35, 13.59) * mm, "end": v(-28.35, 12.2) * mm});
            skLineSegment(sketch, "E343", {"start": v(4.74, 14.27) * mm, "end": v(4.73, 15.77) * mm});
            skLineSegment(sketch, "E344", {"start": v(4.73, 15.77) * mm, "end": v(3.44, 15.76) * mm});
            skLineSegment(sketch, "E345", {"start": v(3.44, 15.76) * mm, "end": v(3.44, 14.27) * mm});
            skLineSegment(sketch, "E346", {"start": v(3.44, 14.27) * mm, "end": v(4.74, 14.27) * mm});
            skLineSegment(sketch, "E347", {"start": v(4.64, -8.33) * mm, "end": v(3.16, -8.33) * mm});
            skLineSegment(sketch, "E348", {"start": v(3.16, -8.33) * mm, "end": v(3.15, -7.04) * mm});
            skLineSegment(sketch, "E349", {"start": v(3.15, -7.04) * mm, "end": v(4.64, -7.04) * mm});
            skLineSegment(sketch, "E350", {"start": v(4.64, -7.04) * mm, "end": v(4.64, -8.33) * mm});
            skLineSegment(sketch, "E351", {"start": v(-3.66, 2.7) * mm, "end": v(-5.48, 2.7) * mm});
            skLineSegment(sketch, "E352", {"start": v(-5.48, 2.7) * mm, "end": v(-5.48, 3.6) * mm});
            skLineSegment(sketch, "E353", {"start": v(-5.48, 3.6) * mm, "end": v(-3.66, 3.62) * mm});
            skLineSegment(sketch, "E354", {"start": v(-3.66, 3.62) * mm, "end": v(-3.66, 2.7) * mm});
            skLineSegment(sketch, "E355", {"start": v(-3.67, 4.38) * mm, "end": v(-5.44, 4.38) * mm});
            skLineSegment(sketch, "E356", {"start": v(-5.44, 4.38) * mm, "end": v(-5.45, 5.3) * mm});
            skLineSegment(sketch, "E357", {"start": v(-5.45, 5.3) * mm, "end": v(-3.67, 5.3) * mm});
            skLineSegment(sketch, "E358", {"start": v(-3.67, 5.3) * mm, "end": v(-3.67, 4.38) * mm});
            skLineSegment(sketch, "E359", {"start": v(-3.67, 6.07) * mm, "end": v(-5.42, 6.06) * mm});
            skLineSegment(sketch, "E360", {"start": v(-5.42, 6.06) * mm, "end": v(-5.42, 6.93) * mm});
            skLineSegment(sketch, "E361", {"start": v(-5.42, 6.93) * mm, "end": v(-3.67, 6.94) * mm});
            skLineSegment(sketch, "E362", {"start": v(-3.67, 6.94) * mm, "end": v(-3.67, 6.07) * mm});
            skLineSegment(sketch, "E363", {"start": v(2.54, 4.1) * mm, "end": v(2.54, 4.2) * mm});
            skLineSegment(sketch, "E364", {"start": v(2.54, 5.36) * mm, "end": v(2.54, 5.6) * mm});
            skLineSegment(sketch, "E365", {"start": v(-1.5, 7.73) * mm, "end": v(-1.5, 7.97) * mm});
            skLineSegment(sketch, "E366", {"start": v(1.06, 5.19) * mm, "end": v(1.06, 5.6) * mm});
            skLineSegment(sketch, "E367", {"start": v(-1.5, 8.32) * mm, "end": v(-1.5, 8.76) * mm});
            skLineSegment(sketch, "E368", {"start": v(1.06, 4.68) * mm, "end": v(0.14, 5.38) * mm});
            skLineSegment(sketch, "E369", {"start": v(0.14, 5.38) * mm, "end": v(0.14, 7.04) * mm});
            skLineSegment(sketch, "E370", {"start": v(0.14, 7.04) * mm, "end": v(-0.87, 7.97) * mm});
            skLineSegment(sketch, "E371", {"start": v(1.06, 4.1) * mm, "end": v(1.06, 4.68) * mm});
            skSolve(sketch);
        }
        {
            var Q0;
            {var subQ3=sQuery(id+"F0.wireOp",EDGE,"E67.bottom");Q0=makeQuery(id+"F0.imprint","IMPRINT",FACE,{"disambiguationData":[TD([[makeQuery(id+"F0.imprint","IMPRINT",EDGE,{"derivedFrom":subQ3}),-1.0]])]});}
            var Q1;
            {var subQ1=sQuery(id+"F0.wireOp",EDGE,"E66.bottom");Q1=makeQuery(id+"F0.imprint","IMPRINT",FACE,{"disambiguationData":[TD([[makeQuery(id+"F0.imprint","IMPRINT",EDGE,{"derivedFrom":subQ1}),-1.0]])]});}
            var Q2;
            {var subQ1=sQuery(id+"F0.wireOp",EDGE,"E65.bottom");Q2=makeQuery(id+"F0.imprint","IMPRINT",FACE,{"disambiguationData":[TD([[makeQuery(id+"F0.imprint","IMPRINT",EDGE,{"derivedFrom":subQ1}),-1.0]])]});}
            var Q3;
            {var subQ3=sQuery(id+"F0.wireOp",EDGE,"E4.bottom");Q3=makeQuery(id+"F0.imprint","IMPRINT",FACE,{"disambiguationData":[TD([[makeQuery(id+"F0.imprint","IMPRINT",EDGE,{"derivedFrom":subQ3}),-1.0]])]});}
            var Q4;
            {var subQ3=sQuery(id+"F0.wireOp",EDGE,"E42.bottom");Q4=makeQuery(id+"F0.imprint","IMPRINT",FACE,{"disambiguationData":[TD([[makeQuery(id+"F0.imprint","IMPRINT",EDGE,{"derivedFrom":subQ3}),-1.0]])]});}
            var Q5;
            {var subQ3=sQuery(id+"F0.wireOp",EDGE,"E68.bottom");Q5=makeQuery(id+"F0.imprint","IMPRINT",FACE,{"disambiguationData":[TD([[makeQuery(id+"F0.imprint","IMPRINT",EDGE,{"derivedFrom":subQ3}),-1.0]])]});}
            var Q6;
            {var subQ3=sQuery(id+"F0.wireOp",EDGE,"E1.bottom");Q6=makeQuery(id+"F0.imprint","IMPRINT",FACE,{"disambiguationData":[TD([[makeQuery(id+"F0.imprint","IMPRINT",EDGE,{"derivedFrom":subQ3}),-1.0]])]});}
            var Q7;
            Q7=makeQuery(id+"F0.imprint","IMPRINT",FACE,{"disambiguationData":[TD([[makeQuery(id+"F0.imprint","IMPRINT",EDGE,{"derivedFrom":sQuery(id+"F0.wireOp",EDGE,"E69.bottom")}),-1.0]])]});
            var Q8;
            Q8=makeQuery(id+"F0.imprint","IMPRINT",FACE,{"disambiguationData":[TD([[makeQuery(id+"F0.imprint","IMPRINT",EDGE,{"derivedFrom":sQuery(id+"F0.wireOp",EDGE,"E40.bottom")}),-1.0]])]});
            var Q9;
            {var subQ3=sQuery(id+"F0.wireOp",EDGE,"E3.bottom");Q9=makeQuery(id+"F0.imprint","IMPRINT",FACE,{"disambiguationData":[TD([[makeQuery(id+"F0.imprint","IMPRINT",EDGE,{"derivedFrom":subQ3}),-1.0]])]});}
            var Q10;
            {var subQ3=sQuery(id+"F0.wireOp",EDGE,"E43.bottom");Q10=makeQuery(id+"F0.imprint","IMPRINT",FACE,{"disambiguationData":[TD([[makeQuery(id+"F0.imprint","IMPRINT",EDGE,{"derivedFrom":subQ3}),-1.0]])]});}
            var Q11;
            Q11=makeQuery(id+"F0.imprint","IMPRINT",FACE,{"disambiguationData":[TD([[makeQuery(id+"F0.imprint","IMPRINT",EDGE,{"derivedFrom":sQuery(id+"F0.wireOp",EDGE,"E38.bottom")}),-1.0]])]});
            var Q12;
            {var subQ3=sQuery(id+"F0.wireOp",EDGE,"E2.bottom");Q12=makeQuery(id+"F0.imprint","IMPRINT",FACE,{"disambiguationData":[TD([[makeQuery(id+"F0.imprint","IMPRINT",EDGE,{"derivedFrom":subQ3}),-1.0]])]});}
            var Q13;
            {var subQ1=sQuery(id+"F0.wireOp",EDGE,"E39.bottom");Q13=makeQuery(id+"F0.imprint","IMPRINT",FACE,{"disambiguationData":[TD([[makeQuery(id+"F0.imprint","IMPRINT",EDGE,{"derivedFrom":subQ1}),-1.0]])]});}
            var Q14;
            {var subQ3=sQuery(id+"F0.wireOp",EDGE,"E64.bottom");Q14=makeQuery(id+"F0.imprint","IMPRINT",FACE,{"disambiguationData":[TD([[makeQuery(id+"F0.imprint","IMPRINT",EDGE,{"derivedFrom":subQ3}),-1.0]])]});}
            var Q15;
            {var subQ3=sQuery(id+"F0.wireOp",EDGE,"E41.bottom");Q15=makeQuery(id+"F0.imprint","IMPRINT",FACE,{"disambiguationData":[TD([[makeQuery(id+"F0.imprint","IMPRINT",EDGE,{"derivedFrom":subQ3}),-1.0]])]});}
            var Q16;
            Q16=makeQuery(id+"F0.imprint","IMPRINT",FACE,{"disambiguationData":[TD([[makeQuery(id+"F0.imprint","IMPRINT",EDGE,{"derivedFrom":sQuery(id+"F0.wireOp",EDGE,"E153")}),1.0]])]});
            var Q17;
            Q17=makeQuery(id+"F0.imprint","IMPRINT",FACE,{"disambiguationData":[TD([[makeQuery(id+"F0.imprint","IMPRINT",EDGE,{"derivedFrom":sQuery(id+"F0.wireOp",EDGE,"E149")}),1.0]])]});
            var Q18;
            Q18=makeQuery(id+"F0.imprint","IMPRINT",FACE,{"disambiguationData":[TD([[makeQuery(id+"F0.imprint","IMPRINT",EDGE,{"derivedFrom":sQuery(id+"F0.wireOp",EDGE,"E137")}),-1.0]])]});
            var Q19;
            {var subQ0=sQuery(id+"F0.wireOp",EDGE,"E117");Q19=makeQuery(id+"F0.imprint","IMPRINT",FACE,{"disambiguationData":[TD([[makeQuery(id+"F0.imprint","IMPRINT",EDGE,{"derivedFrom":subQ0}),-1.0]])]});}
            var Q20;
            Q20=makeQuery(id+"F0.imprint","IMPRINT",FACE,{"disambiguationData":[TD([[makeQuery(id+"F0.imprint","IMPRINT",EDGE,{"derivedFrom":sQuery(id+"F0.wireOp",EDGE,"E73")}),-1.0]])]});
            var Q21;
            {var subQ0=sQuery(id+"F0.wireOp",EDGE,"E121");Q21=makeQuery(id+"F0.imprint","IMPRINT",FACE,{"disambiguationData":[TD([[makeQuery(id+"F0.imprint","IMPRINT",EDGE,{"derivedFrom":subQ0}),-1.0]])]});}
            var Q22;
            {var subQ0=sQuery(id+"F0.wireOp",EDGE,"E107");Q22=makeQuery(id+"F0.imprint","IMPRINT",FACE,{"disambiguationData":[TD([[makeQuery(id+"F0.imprint","IMPRINT",EDGE,{"derivedFrom":subQ0}),1.0]])]});}
            var Q23;
            Q23=makeQuery(id+"F0.imprint","IMPRINT",FACE,{"disambiguationData":[TD([[makeQuery(id+"F0.imprint","IMPRINT",EDGE,{"derivedFrom":sQuery(id+"F0.wireOp",EDGE,"E77")}),-1.0]])]});
            var Q24;
            Q24=makeQuery(id+"F0.imprint","IMPRINT",FACE,{"disambiguationData":[TD([[makeQuery(id+"F0.imprint","IMPRINT",EDGE,{"derivedFrom":sQuery(id+"F0.wireOp",EDGE,"E186")}),1.0]])]});
            var Q25;
            Q25=makeQuery(id+"F0.imprint","IMPRINT",FACE,{"disambiguationData":[TD([[makeQuery(id+"F0.imprint","IMPRINT",EDGE,{"derivedFrom":sQuery(id+"F0.wireOp",EDGE,"E102")}),-1.0]])]});
            var Q26;
            Q26=makeQuery(id+"F0.imprint","IMPRINT",FACE,{"disambiguationData":[TD([[makeQuery(id+"F0.imprint","IMPRINT",EDGE,{"derivedFrom":sQuery(id+"F0.wireOp",EDGE,"E266")}),1.0]])]});
            var Q27;
            Q27=makeQuery(id+"F0.imprint","IMPRINT",FACE,{"disambiguationData":[TD([[makeQuery(id+"F0.imprint","IMPRINT",EDGE,{"derivedFrom":sQuery(id+"F0.wireOp",EDGE,"E10.top")}),1.0]])]});
            var Q28;
            Q28=makeQuery(id+"F0.imprint","IMPRINT",FACE,{"disambiguationData":[TD([[makeQuery(id+"F0.imprint","IMPRINT",EDGE,{"derivedFrom":sQuery(id+"F0.wireOp",EDGE,"E51.bottom")}),-1.0]])]});
            var Q29;
            {var subQ1=sQuery(id+"F0.wireOp",EDGE,"E35.bottom");Q29=makeQuery(id+"F0.imprint","IMPRINT",FACE,{"disambiguationData":[TD([[makeQuery(id+"F0.imprint","IMPRINT",EDGE,{"derivedFrom":subQ1}),-1.0]])]});}
            var Q30;
            {var subQ1=sQuery(id+"F0.wireOp",EDGE,"E31.bottom");Q30=makeQuery(id+"F0.imprint","IMPRINT",FACE,{"disambiguationData":[TD([[makeQuery(id+"F0.imprint","IMPRINT",EDGE,{"derivedFrom":subQ1}),-1.0]])]});}
            var Q31;
            Q31=makeQuery(id+"F0.imprint","IMPRINT",FACE,{"disambiguationData":[TD([[makeQuery(id+"F0.imprint","IMPRINT",EDGE,{"derivedFrom":sQuery(id+"F0.wireOp",EDGE,"E343")}),1.0]])]});
            var Q32;
            Q32=makeQuery(id+"F0.imprint","IMPRINT",FACE,{"disambiguationData":[TD([[makeQuery(id+"F0.imprint","IMPRINT",EDGE,{"derivedFrom":sQuery(id+"F0.wireOp",EDGE,"E250")}),-1.0]])]});
            var Q33;
            Q33=makeQuery(id+"F0.imprint","IMPRINT",FACE,{"disambiguationData":[TD([[makeQuery(id+"F0.imprint","IMPRINT",EDGE,{"derivedFrom":sQuery(id+"F0.wireOp",EDGE,"E339")}),-1.0]])]});
            var Q34;
            Q34=makeQuery(id+"F0.imprint","IMPRINT",FACE,{"disambiguationData":[TD([[makeQuery(id+"F0.imprint","IMPRINT",EDGE,{"derivedFrom":sQuery(id+"F0.wireOp",EDGE,"E254")}),-1.0]])]});
            var Q35;
            Q35=makeQuery(id+"F0.imprint","IMPRINT",FACE,{"disambiguationData":[TD([[makeQuery(id+"F0.imprint","IMPRINT",EDGE,{"derivedFrom":sQuery(id+"F0.wireOp",EDGE,"E48.top")}),1.0]])]});
            var Q36;
            Q36=makeQuery(id+"F0.imprint","IMPRINT",FACE,{"disambiguationData":[TD([[makeQuery(id+"F0.imprint","IMPRINT",EDGE,{"derivedFrom":sQuery(id+"F0.wireOp",EDGE,"E258")}),-1.0]])]});
            var Q37;
            Q37=makeQuery(id+"F0.imprint","IMPRINT",FACE,{"disambiguationData":[TD([[makeQuery(id+"F0.imprint","IMPRINT",EDGE,{"derivedFrom":sQuery(id+"F0.wireOp",EDGE,"E14.bottom")}),-1.0]])]});
            var Q38;
            {var subQ1=sQuery(id+"F0.wireOp",EDGE,"E50.top");Q38=makeQuery(id+"F0.imprint","IMPRINT",FACE,{"disambiguationData":[TD([[makeQuery(id+"F0.imprint","IMPRINT",EDGE,{"derivedFrom":subQ1}),1.0]])]});}
            var Q39;
            Q39=makeQuery(id+"F0.imprint","IMPRINT",FACE,{"disambiguationData":[TD([[makeQuery(id+"F0.imprint","IMPRINT",EDGE,{"derivedFrom":sQuery(id+"F0.wireOp",EDGE,"E230")}),-1.0]])]});
            var Q40;
            {var subQ1=sQuery(id+"F0.wireOp",EDGE,"E27.bottom");Q40=makeQuery(id+"F0.imprint","IMPRINT",FACE,{"disambiguationData":[TD([[makeQuery(id+"F0.imprint","IMPRINT",EDGE,{"derivedFrom":subQ1}),-1.0]])]});}
            var Q41;
            Q41=makeQuery(id+"F0.imprint","IMPRINT",FACE,{"disambiguationData":[TD([[makeQuery(id+"F0.imprint","IMPRINT",EDGE,{"derivedFrom":sQuery(id+"F0.wireOp",EDGE,"E319")}),-1.0]])]});
            var Q42;
            {var subQ3=sQuery(id+"F0.wireOp",EDGE,"E28.bottom");Q42=makeQuery(id+"F0.imprint","IMPRINT",FACE,{"disambiguationData":[TD([[makeQuery(id+"F0.imprint","IMPRINT",EDGE,{"derivedFrom":subQ3}),-1.0]])]});}
            var Q43;
            {var subQ1=sQuery(id+"F0.wireOp",EDGE,"E6.bottom");Q43=makeQuery(id+"F0.imprint","IMPRINT",FACE,{"disambiguationData":[TD([[makeQuery(id+"F0.imprint","IMPRINT",EDGE,{"derivedFrom":subQ1}),-1.0]])]});}
            var Q44;
            {var subQ3=sQuery(id+"F0.wireOp",EDGE,"E5.bottom");Q44=makeQuery(id+"F0.imprint","IMPRINT",FACE,{"disambiguationData":[TD([[makeQuery(id+"F0.imprint","IMPRINT",EDGE,{"derivedFrom":subQ3}),-1.0]])]});}
            var Q45;
            Q45=makeQuery(id+"F0.imprint","IMPRINT",FACE,{"disambiguationData":[TD([[makeQuery(id+"F0.imprint","IMPRINT",EDGE,{"derivedFrom":sQuery(id+"F0.wireOp",EDGE,"E25.bottom")}),-1.0]])]});
            var Q46;
            Q46=makeQuery(id+"F0.imprint","IMPRINT",FACE,{"disambiguationData":[TD([[makeQuery(id+"F0.imprint","IMPRINT",EDGE,{"derivedFrom":sQuery(id+"F0.wireOp",EDGE,"E315")}),-1.0]])]});
            var Q47;
            Q47=makeQuery(id+"F0.imprint","IMPRINT",FACE,{"disambiguationData":[TD([[makeQuery(id+"F0.imprint","IMPRINT",EDGE,{"derivedFrom":sQuery(id+"F0.wireOp",EDGE,"E270")}),1.0]])]});
            var Q48;
            Q48=makeQuery(id+"F0.imprint","IMPRINT",FACE,{"disambiguationData":[TD([[makeQuery(id+"F0.imprint","IMPRINT",EDGE,{"derivedFrom":sQuery(id+"F0.wireOp",EDGE,"E45.bottom")}),-1.0]])]});
            var Q49;
            {var subQ3=sQuery(id+"F0.wireOp",EDGE,"E34.bottom");Q49=makeQuery(id+"F0.imprint","IMPRINT",FACE,{"disambiguationData":[TD([[makeQuery(id+"F0.imprint","IMPRINT",EDGE,{"derivedFrom":subQ3}),-1.0]])]});}
            var Q50;
            Q50=makeQuery(id+"F0.imprint","IMPRINT",FACE,{"disambiguationData":[TD([[makeQuery(id+"F0.imprint","IMPRINT",EDGE,{"derivedFrom":sQuery(id+"F0.wireOp",EDGE,"E347")}),-1.0]])]});
            var Q51;
            Q51=makeQuery(id+"F0.imprint","IMPRINT",FACE,{"disambiguationData":[TD([[makeQuery(id+"F0.imprint","IMPRINT",EDGE,{"derivedFrom":sQuery(id+"F0.wireOp",EDGE,"E52.top")}),1.0]])]});
            var Q52;
            Q52=makeQuery(id+"F0.imprint","IMPRINT",FACE,{"disambiguationData":[TD([[makeQuery(id+"F0.imprint","IMPRINT",EDGE,{"derivedFrom":sQuery(id+"F0.wireOp",EDGE,"E22.top")}),1.0]])]});
            var Q53;
            Q53=makeQuery(id+"F0.imprint","IMPRINT",FACE,{"disambiguationData":[TD([[makeQuery(id+"F0.imprint","IMPRINT",EDGE,{"derivedFrom":sQuery(id+"F0.wireOp",EDGE,"E46.top")}),1.0]])]});
            var Q54;
            Q54=makeQuery(id+"F0.imprint","IMPRINT",FACE,{"disambiguationData":[TD([[makeQuery(id+"F0.imprint","IMPRINT",EDGE,{"derivedFrom":sQuery(id+"F0.wireOp",EDGE,"E24.bottom")}),-1.0]])]});
            var Q55;
            Q55=makeQuery(id+"F0.imprint","IMPRINT",FACE,{"disambiguationData":[TD([[makeQuery(id+"F0.imprint","IMPRINT",EDGE,{"derivedFrom":sQuery(id+"F0.wireOp",EDGE,"E327")}),-1.0]])]});
            var Q56;
            {var subQ3=sQuery(id+"F0.wireOp",EDGE,"E9.bottom");Q56=makeQuery(id+"F0.imprint","IMPRINT",FACE,{"disambiguationData":[TD([[makeQuery(id+"F0.imprint","IMPRINT",EDGE,{"derivedFrom":subQ3}),-1.0]])]});}
            var Q57;
            Q57=makeQuery(id+"F0.imprint","IMPRINT",FACE,{"disambiguationData":[TD([[makeQuery(id+"F0.imprint","IMPRINT",EDGE,{"derivedFrom":sQuery(id+"F0.wireOp",EDGE,"E47.bottom")}),-1.0]])]});
            var Q58;
            {var subQ3=sQuery(id+"F0.wireOp",EDGE,"E7.bottom");Q58=makeQuery(id+"F0.imprint","IMPRINT",FACE,{"disambiguationData":[TD([[makeQuery(id+"F0.imprint","IMPRINT",EDGE,{"derivedFrom":subQ3}),-1.0]])]});}
            var Q59;
            {var subQ3=sQuery(id+"F0.wireOp",EDGE,"E21.bottom");Q59=makeQuery(id+"F0.imprint","IMPRINT",FACE,{"disambiguationData":[TD([[makeQuery(id+"F0.imprint","IMPRINT",EDGE,{"derivedFrom":subQ3}),-1.0]])]});}
            var Q60;
            Q60=makeQuery(id+"F0.imprint","IMPRINT",FACE,{"disambiguationData":[TD([[makeQuery(id+"F0.imprint","IMPRINT",EDGE,{"derivedFrom":sQuery(id+"F0.wireOp",EDGE,"E308")}),1.0]])]});
            var Q61;
            {var subQ1=sQuery(id+"F0.wireOp",EDGE,"E53.bottom");Q61=makeQuery(id+"F0.imprint","IMPRINT",FACE,{"disambiguationData":[TD([[makeQuery(id+"F0.imprint","IMPRINT",EDGE,{"derivedFrom":subQ1}),-1.0]])]});}
            var Q62;
            Q62=makeQuery(id+"F0.imprint","IMPRINT",FACE,{"disambiguationData":[TD([[makeQuery(id+"F0.imprint","IMPRINT",EDGE,{"derivedFrom":sQuery(id+"F0.wireOp",EDGE,"E62.top")}),1.0]])]});
            var Q63;
            {var subQ1=sQuery(id+"F0.wireOp",EDGE,"E29.bottom");Q63=makeQuery(id+"F0.imprint","IMPRINT",FACE,{"disambiguationData":[TD([[makeQuery(id+"F0.imprint","IMPRINT",EDGE,{"derivedFrom":subQ1}),-1.0]])]});}
            var Q64;
            Q64=makeQuery(id+"F0.imprint","IMPRINT",FACE,{"disambiguationData":[TD([[makeQuery(id+"F0.imprint","IMPRINT",EDGE,{"derivedFrom":sQuery(id+"F0.wireOp",EDGE,"E323")}),1.0]])]});
            var Q65;
            {var subQ3=sQuery(id+"F0.wireOp",EDGE,"E26.bottom");Q65=makeQuery(id+"F0.imprint","IMPRINT",FACE,{"disambiguationData":[TD([[makeQuery(id+"F0.imprint","IMPRINT",EDGE,{"derivedFrom":subQ3}),-1.0]])]});}
            var Q66;
            Q66=makeQuery(id+"F0.imprint","IMPRINT",FACE,{"disambiguationData":[TD([[makeQuery(id+"F0.imprint","IMPRINT",EDGE,{"derivedFrom":sQuery(id+"F0.wireOp",EDGE,"E208")}),-1.0]])]});
            var Q67;
            {var subQ1=sQuery(id+"F0.wireOp",EDGE,"E55.bottom");Q67=makeQuery(id+"F0.imprint","IMPRINT",FACE,{"disambiguationData":[TD([[makeQuery(id+"F0.imprint","IMPRINT",EDGE,{"derivedFrom":subQ1}),-1.0]])]});}
            var Q68;
            Q68=makeQuery(id+"F0.imprint","IMPRINT",FACE,{"disambiguationData":[TD([[makeQuery(id+"F0.imprint","IMPRINT",EDGE,{"derivedFrom":sQuery(id+"F0.wireOp",EDGE,"E351")}),-1.0]])]});
            var Q69;
            {var subQ3=sQuery(id+"F0.wireOp",EDGE,"E32.bottom");Q69=makeQuery(id+"F0.imprint","IMPRINT",FACE,{"disambiguationData":[TD([[makeQuery(id+"F0.imprint","IMPRINT",EDGE,{"derivedFrom":subQ3}),-1.0]])]});}
            var Q70;
            Q70=makeQuery(id+"F0.imprint","IMPRINT",FACE,{"disambiguationData":[TD([[makeQuery(id+"F0.imprint","IMPRINT",EDGE,{"derivedFrom":sQuery(id+"F0.wireOp",EDGE,"E262")}),-1.0]])]});
            var Q71;
            Q71=makeQuery(id+"F0.imprint","IMPRINT",FACE,{"disambiguationData":[TD([[makeQuery(id+"F0.imprint","IMPRINT",EDGE,{"derivedFrom":sQuery(id+"F0.wireOp",EDGE,"E359")}),-1.0]])]});
            var Q72;
            Q72=makeQuery(id+"F0.imprint","IMPRINT",FACE,{"disambiguationData":[TD([[makeQuery(id+"F0.imprint","IMPRINT",EDGE,{"derivedFrom":sQuery(id+"F0.wireOp",EDGE,"E278")}),-1.0]])]});
            var Q73;
            Q73=makeQuery(id+"F0.imprint","IMPRINT",FACE,{"disambiguationData":[TD([[makeQuery(id+"F0.imprint","IMPRINT",EDGE,{"derivedFrom":sQuery(id+"F0.wireOp",EDGE,"E37.bottom")}),-1.0]])]});
            var Q74;
            {var subQ0=sQuery(id+"F0.wireOp",EDGE,"E227");Q74=makeQuery(id+"F0.imprint","IMPRINT",FACE,{"disambiguationData":[TD([[makeQuery(id+"F0.imprint","IMPRINT",EDGE,{"derivedFrom":subQ0}),1.0]])]});}
            var Q75;
            Q75=makeQuery(id+"F0.imprint","IMPRINT",FACE,{"disambiguationData":[TD([[makeQuery(id+"F0.imprint","IMPRINT",EDGE,{"derivedFrom":sQuery(id+"F0.wireOp",EDGE,"E204")}),-1.0]])]});
            var Q76;
            {var subQ3=sQuery(id+"F0.wireOp",EDGE,"E13.bottom");Q76=makeQuery(id+"F0.imprint","IMPRINT",FACE,{"disambiguationData":[TD([[makeQuery(id+"F0.imprint","IMPRINT",EDGE,{"derivedFrom":subQ3}),-1.0]])]});}
            var Q77;
            Q77=makeQuery(id+"F0.imprint","IMPRINT",FACE,{"disambiguationData":[TD([[makeQuery(id+"F0.imprint","IMPRINT",EDGE,{"derivedFrom":sQuery(id+"F0.wireOp",EDGE,"E335")}),-1.0]])]});
            var Q78;
            {var subQ2=sQuery(id+"F0.wireOp",EDGE,"E312");Q78=makeQuery(id+"F0.imprint","IMPRINT",FACE,{"disambiguationData":[TD([[makeQuery(id+"F0.imprint","IMPRINT",EDGE,{"derivedFrom":subQ2}),1.0]])]});}
            var Q79;
            Q79=makeQuery(id+"F0.imprint","IMPRINT",FACE,{"disambiguationData":[TD([[makeQuery(id+"F0.imprint","IMPRINT",EDGE,{"derivedFrom":sQuery(id+"F0.wireOp",EDGE,"E49.bottom")}),-1.0]])]});
            var Q80;
            Q80=makeQuery(id+"F0.imprint","IMPRINT",FACE,{"disambiguationData":[TD([[makeQuery(id+"F0.imprint","IMPRINT",EDGE,{"derivedFrom":sQuery(id+"F0.wireOp",EDGE,"E54.top")}),1.0]])]});
            var Q81;
            {var subQ3=sQuery(id+"F0.wireOp",EDGE,"E30.bottom");Q81=makeQuery(id+"F0.imprint","IMPRINT",FACE,{"disambiguationData":[TD([[makeQuery(id+"F0.imprint","IMPRINT",EDGE,{"derivedFrom":subQ3}),-1.0]])]});}
            var Q82;
            Q82=makeQuery(id+"F0.imprint","IMPRINT",FACE,{"disambiguationData":[TD([[makeQuery(id+"F0.imprint","IMPRINT",EDGE,{"derivedFrom":sQuery(id+"F0.wireOp",EDGE,"E246")}),-1.0]])]});
            var Q83;
            {var subQ0=sQuery(id+"F0.wireOp",EDGE,"E242");Q83=makeQuery(id+"F0.imprint","IMPRINT",FACE,{"disambiguationData":[TD([[makeQuery(id+"F0.imprint","IMPRINT",EDGE,{"derivedFrom":subQ0}),1.0]])]});}
            var Q84;
            Q84=makeQuery(id+"F0.imprint","IMPRINT",FACE,{"disambiguationData":[TD([[makeQuery(id+"F0.imprint","IMPRINT",EDGE,{"derivedFrom":sQuery(id+"F0.wireOp",EDGE,"E331")}),-1.0]])]});
            var Q85;
            Q85=makeQuery(id+"F0.imprint","IMPRINT",FACE,{"disambiguationData":[TD([[makeQuery(id+"F0.imprint","IMPRINT",EDGE,{"derivedFrom":sQuery(id+"F0.wireOp",EDGE,"E129")}),1.0]])]});
            var Q86;
            {var subQ3=sQuery(id+"F0.wireOp",EDGE,"E63.bottom");Q86=makeQuery(id+"F0.imprint","IMPRINT",FACE,{"disambiguationData":[TD([[makeQuery(id+"F0.imprint","IMPRINT",EDGE,{"derivedFrom":subQ3}),-1.0]])]});}
            var Q87;
            Q87=makeQuery(id+"F0.imprint","IMPRINT",FACE,{"disambiguationData":[TD([[makeQuery(id+"F0.imprint","IMPRINT",EDGE,{"derivedFrom":sQuery(id+"F0.wireOp",EDGE,"E216")}),-1.0]])]});
            var Q88;
            Q88=makeQuery(id+"F0.imprint","IMPRINT",FACE,{"disambiguationData":[TD([[makeQuery(id+"F0.imprint","IMPRINT",EDGE,{"derivedFrom":sQuery(id+"F0.wireOp",EDGE,"E60.right")}),1.0]])]});
            var Q89;
            {var subQ1=sQuery(id+"F0.wireOp",EDGE,"E23.bottom");Q89=makeQuery(id+"F0.imprint","IMPRINT",FACE,{"disambiguationData":[TD([[makeQuery(id+"F0.imprint","IMPRINT",EDGE,{"derivedFrom":subQ1}),-1.0]])]});}
            var Q90;
            Q90=makeQuery(id+"F0.imprint","IMPRINT",FACE,{"disambiguationData":[TD([[makeQuery(id+"F0.imprint","IMPRINT",EDGE,{"derivedFrom":sQuery(id+"F0.wireOp",EDGE,"E212")}),1.0]])]});
            var Q91;
            {var subQ3=sQuery(id+"F0.wireOp",EDGE,"E11.bottom");Q91=makeQuery(id+"F0.imprint","IMPRINT",FACE,{"disambiguationData":[TD([[makeQuery(id+"F0.imprint","IMPRINT",EDGE,{"derivedFrom":subQ3}),-1.0]])]});}
            var Q92;
            Q92=makeQuery(id+"F0.imprint","IMPRINT",FACE,{"disambiguationData":[TD([[makeQuery(id+"F0.imprint","IMPRINT",EDGE,{"derivedFrom":sQuery(id+"F0.wireOp",EDGE,"E282")}),-1.0]])]});
            var Q93;
            Q93=makeQuery(id+"F0.imprint","IMPRINT",FACE,{"disambiguationData":[TD([[makeQuery(id+"F0.imprint","IMPRINT",EDGE,{"derivedFrom":sQuery(id+"F0.wireOp",EDGE,"E203")}),-1.0]])]});
            var Q94;
            Q94=makeQuery(id+"F0.imprint","IMPRINT",FACE,{"disambiguationData":[TD([[makeQuery(id+"F0.imprint","IMPRINT",EDGE,{"derivedFrom":sQuery(id+"F0.wireOp",EDGE,"E94")}),-1.0]])]});
            var Q95;
            Q95=makeQuery(id+"F0.imprint","IMPRINT",FACE,{"disambiguationData":[TD([[makeQuery(id+"F0.imprint","IMPRINT",EDGE,{"derivedFrom":sQuery(id+"F0.wireOp",EDGE,"E274")}),-1.0]])]});
            var Q96;
            Q96=makeQuery(id+"F0.imprint","IMPRINT",FACE,{"disambiguationData":[TD([[makeQuery(id+"F0.imprint","IMPRINT",EDGE,{"derivedFrom":sQuery(id+"F0.wireOp",EDGE,"E202")}),1.0]])]});
            var Q97;
            Q97=makeQuery(id+"F0.imprint","IMPRINT",FACE,{"disambiguationData":[TD([[makeQuery(id+"F0.imprint","IMPRINT",EDGE,{"derivedFrom":sQuery(id+"F0.wireOp",EDGE,"E58.left")}),-1.0]])]});
            var Q98;
            Q98=makeQuery(id+"F0.imprint","IMPRINT",FACE,{"disambiguationData":[TD([[makeQuery(id+"F0.imprint","IMPRINT",EDGE,{"derivedFrom":sQuery(id+"F0.wireOp",EDGE,"E20.top")}),1.0]])]});
            var Q99;
            {var subQ1=sQuery(id+"F0.wireOp",EDGE,"E8.bottom");Q99=makeQuery(id+"F0.imprint","IMPRINT",FACE,{"disambiguationData":[TD([[makeQuery(id+"F0.imprint","IMPRINT",EDGE,{"derivedFrom":subQ1}),-1.0]])]});}
            var Q100;
            Q100=makeQuery(id+"F0.imprint","IMPRINT",FACE,{"disambiguationData":[TD([[makeQuery(id+"F0.imprint","IMPRINT",EDGE,{"derivedFrom":sQuery(id+"F0.wireOp",EDGE,"E19.bottom")}),-1.0]])]});
            var Q101;
            {var subQ1=sQuery(id+"F0.wireOp",EDGE,"E33.bottom");Q101=makeQuery(id+"F0.imprint","IMPRINT",FACE,{"disambiguationData":[TD([[makeQuery(id+"F0.imprint","IMPRINT",EDGE,{"derivedFrom":subQ1}),-1.0]])]});}
            var Q102;
            Q102=makeQuery(id+"F0.imprint","IMPRINT",FACE,{"disambiguationData":[TD([[makeQuery(id+"F0.imprint","IMPRINT",EDGE,{"derivedFrom":sQuery(id+"F0.wireOp",EDGE,"E57.left")}),-1.0]])]});
            var Q103;
            Q103=makeQuery(id+"F0.imprint","IMPRINT",FACE,{"disambiguationData":[TD([[makeQuery(id+"F0.imprint","IMPRINT",EDGE,{"derivedFrom":sQuery(id+"F0.wireOp",EDGE,"E178")}),1.0]])]});
            var Q104;
            {var subQ0=sQuery(id+"F0.wireOp",EDGE,"E12.left");Q104=makeQuery(id+"F0.imprint","IMPRINT",FACE,{"disambiguationData":[TD([[makeQuery(id+"F0.imprint","IMPRINT",EDGE,{"derivedFrom":subQ0}),1.0]])]});}
            var Q105;
            Q105=makeQuery(id+"F0.imprint","IMPRINT",FACE,{"disambiguationData":[TD([[makeQuery(id+"F0.imprint","IMPRINT",EDGE,{"derivedFrom":sQuery(id+"F0.wireOp",EDGE,"E61.bottom")}),-1.0]])]});
            var Q106;
            Q106=makeQuery(id+"F0.imprint","IMPRINT",FACE,{"disambiguationData":[TD([[makeQuery(id+"F0.imprint","IMPRINT",EDGE,{"derivedFrom":sQuery(id+"F0.wireOp",EDGE,"E170")}),-1.0]])]});
            var Q107;
            Q107=makeQuery(id+"F0.imprint","IMPRINT",FACE,{"disambiguationData":[TD([[makeQuery(id+"F0.imprint","IMPRINT",EDGE,{"derivedFrom":sQuery(id+"F0.wireOp",EDGE,"E93")}),1.0]])]});
            var Q108;
            Q108=makeQuery(id+"F0.imprint","IMPRINT",FACE,{"disambiguationData":[TD([[makeQuery(id+"F0.imprint","IMPRINT",EDGE,{"derivedFrom":sQuery(id+"F0.wireOp",EDGE,"E15.top")}),1.0]])]});
            var Q109;
            Q109=makeQuery(id+"F0.imprint","IMPRINT",FACE,{"disambiguationData":[TD([[makeQuery(id+"F0.imprint","IMPRINT",EDGE,{"derivedFrom":sQuery(id+"F0.wireOp",EDGE,"E18.bottom")}),-1.0]])]});
            var Q110;
            Q110=makeQuery(id+"F0.imprint","IMPRINT",FACE,{"disambiguationData":[TD([[makeQuery(id+"F0.imprint","IMPRINT",EDGE,{"derivedFrom":sQuery(id+"F0.wireOp",EDGE,"E125")}),-1.0]])]});
            var Q111;
            Q111=makeQuery(id+"F0.imprint","IMPRINT",FACE,{"disambiguationData":[TD([[makeQuery(id+"F0.imprint","IMPRINT",EDGE,{"derivedFrom":sQuery(id+"F0.wireOp",EDGE,"E355")}),-1.0]])]});
            var Q112;
            {var subQ3=sQuery(id+"F0.wireOp",EDGE,"E36.bottom");Q112=makeQuery(id+"F0.imprint","IMPRINT",FACE,{"disambiguationData":[TD([[makeQuery(id+"F0.imprint","IMPRINT",EDGE,{"derivedFrom":subQ3}),-1.0]])]});}
            var Q113;
            Q113=makeQuery(id+"F0.imprint","IMPRINT",FACE,{"disambiguationData":[TD([[makeQuery(id+"F0.imprint","IMPRINT",EDGE,{"derivedFrom":sQuery(id+"F0.wireOp",EDGE,"E56.bottom")}),-1.0]])]});
            var Q114;
            {var subQ0=sQuery(id+"F0.wireOp",EDGE,"E124");Q114=makeQuery(id+"F0.imprint","IMPRINT",FACE,{"disambiguationData":[TD([[makeQuery(id+"F0.imprint","IMPRINT",EDGE,{"derivedFrom":subQ0}),-1.0]])]});}
            var Q115;
            Q115=makeQuery(id+"F0.imprint","IMPRINT",FACE,{"disambiguationData":[TD([[makeQuery(id+"F0.imprint","IMPRINT",EDGE,{"derivedFrom":sQuery(id+"F0.wireOp",EDGE,"E190")}),1.0]])]});
            var Q116;
            Q116=makeQuery(id+"F0.imprint","IMPRINT",FACE,{"disambiguationData":[TD([[makeQuery(id+"F0.imprint","IMPRINT",EDGE,{"derivedFrom":sQuery(id+"F0.wireOp",EDGE,"E58.bottom")}),-1.0]])]});
            var Q117;
            {var subQ1=sQuery(id+"F0.wireOp",EDGE,"E17.bottom");Q117=makeQuery(id+"F0.imprint","IMPRINT",FACE,{"disambiguationData":[TD([[makeQuery(id+"F0.imprint","IMPRINT",EDGE,{"derivedFrom":subQ1}),-1.0]])]});}
            var Q118;
            Q118=makeQuery(id+"F0.imprint","IMPRINT",FACE,{"disambiguationData":[TD([[makeQuery(id+"F0.imprint","IMPRINT",EDGE,{"derivedFrom":sQuery(id+"F0.wireOp",EDGE,"E57.bottom")}),-1.0]])]});
            var Q119;
            Q119=makeQuery(id+"F0.imprint","IMPRINT",FACE,{"disambiguationData":[TD([[makeQuery(id+"F0.imprint","IMPRINT",EDGE,{"derivedFrom":sQuery(id+"F0.wireOp",EDGE,"E16.top")}),1.0]])]});
            var Q120;
            Q120=makeQuery(id+"F0.imprint","IMPRINT",FACE,{"disambiguationData":[TD([[makeQuery(id+"F0.imprint","IMPRINT",EDGE,{"derivedFrom":sQuery(id+"F0.wireOp",EDGE,"E60.bottom")}),-1.0]])]});
            var Q121;
            Q121=makeQuery(id+"F0.imprint","IMPRINT",FACE,{"disambiguationData":[TD([[makeQuery(id+"F0.imprint","IMPRINT",EDGE,{"derivedFrom":sQuery(id+"F0.wireOp",EDGE,"E59.top")}),1.0]])]});
            var Q122;
            Q122=makeQuery(id+"F0.imprint","IMPRINT",FACE,{"disambiguationData":[TD([[makeQuery(id+"F0.imprint","IMPRINT",EDGE,{"derivedFrom":sQuery(id+"F0.wireOp",EDGE,"E301")}),-1.0]])]});
            extrude(context, id + "F1", {"entities" : qUnion([Q0, Q1, Q2, Q3, Q4, Q5, Q6, Q7, Q8, Q9, Q10, Q11, Q12, Q13, Q14, Q15, Q16, Q17, Q18, Q19, Q20, Q21, Q22, Q23, Q24, Q25, Q26, Q27, Q28, Q29, Q30, Q31, Q32, Q33, Q34, Q35, Q36, Q37, Q38, Q39, Q40, Q41, Q42, Q43, Q44, Q45, Q46, Q47, Q48, Q49, Q50, Q51, Q52, Q53, Q54, Q55, Q56, Q57, Q58, Q59, Q60, Q61, Q62, Q63, Q64, Q65, Q66, Q67, Q68, Q69, Q70, Q71, Q72, Q73, Q74, Q75, Q76, Q77, Q78, Q79, Q80, Q81, Q82, Q83, Q84, Q85, Q86, Q87, Q88, Q89, Q90, Q91, Q92, Q93, Q94, Q95, Q96, Q97, Q98, Q99, Q100, Q101, Q102, Q103, Q104, Q105, Q106, Q107, Q108, Q109, Q110, Q111, Q112, Q113, Q114, Q115, Q116, Q117, Q118, Q119, Q120, Q121, Q122]), "depth" : 2.54 * mm, "offsetDistance" : 25.4 * mm});
        }
        {
            var Q0;
            Q0=makeQuery(id+"F1.opExtrude","SWEPT_BODY",BODY,{"disambiguationData":[OSD([sQuery(id+"F0.wireOp",EDGE,"E69.bottom"),sQuery(id+"F0.wireOp",EDGE,"E69.top"),sQuery(id+"F0.wireOp",EDGE,"E69.left"),sQuery(id+"F0.wireOp",EDGE,"E69.right")])]});
            var Q1;
            Q1=makeQuery(id+"F1.opExtrude","SWEPT_BODY",BODY,{"disambiguationData":[OSD([sQuery(id+"F0.wireOp",EDGE,"E94"),sQuery(id+"F0.wireOp",EDGE,"E95"),sQuery(id+"F0.wireOp",EDGE,"E96"),sQuery(id+"F0.wireOp",EDGE,"E97"),sQuery(id+"F0.wireOp",EDGE,"E98"),sQuery(id+"F0.wireOp",EDGE,"E99"),sQuery(id+"F0.wireOp",EDGE,"E100"),sQuery(id+"F0.wireOp",EDGE,"E101"),sQuery(id+"F0.wireOp",EDGE,"E234"),sQuery(id+"F0.wireOp",EDGE,"E235"),sQuery(id+"F0.wireOp",EDGE,"E236")])]});
            var Q2;
            Q2=makeQuery(id+"F1.opExtrude","SWEPT_BODY",BODY,{"disambiguationData":[OSD([sQuery(id+"F0.wireOp",EDGE,"E66.bottom"),sQuery(id+"F0.wireOp",EDGE,"E66.top"),sQuery(id+"F0.wireOp",EDGE,"E66.left"),sQuery(id+"F0.wireOp",EDGE,"E66.right"),sQuery(id+"F0.wireOp",EDGE,"E327"),sQuery(id+"F0.wireOp",EDGE,"E328"),sQuery(id+"F0.wireOp",EDGE,"E329")])]});
            var Q3;
            Q3=makeQuery(id+"F1.opExtrude","SWEPT_BODY",BODY,{"disambiguationData":[OSD([sQuery(id+"F0.wireOp",EDGE,"E65.bottom"),sQuery(id+"F0.wireOp",EDGE,"E65.top"),sQuery(id+"F0.wireOp",EDGE,"E65.left"),sQuery(id+"F0.wireOp",EDGE,"E65.right"),sQuery(id+"F0.wireOp",EDGE,"E323"),sQuery(id+"F0.wireOp",EDGE,"E324"),sQuery(id+"F0.wireOp",EDGE,"E325")])]});
            var Q4;
            Q4=makeQuery(id+"F1.opExtrude","SWEPT_BODY",BODY,{"disambiguationData":[OSD([sQuery(id+"F0.wireOp",EDGE,"E64.bottom"),sQuery(id+"F0.wireOp",EDGE,"E64.top"),sQuery(id+"F0.wireOp",EDGE,"E64.left"),sQuery(id+"F0.wireOp",EDGE,"E64.right")])]});
            var Q5;
            Q5=makeQuery(id+"F1.opExtrude","SWEPT_BODY",BODY,{"disambiguationData":[OSD([sQuery(id+"F0.wireOp",EDGE,"E62.bottom"),sQuery(id+"F0.wireOp",EDGE,"E62.top"),sQuery(id+"F0.wireOp",EDGE,"E62.left"),sQuery(id+"F0.wireOp",EDGE,"E62.right"),sQuery(id+"F0.wireOp",EDGE,"E312"),sQuery(id+"F0.wireOp",EDGE,"E313"),sQuery(id+"F0.wireOp",EDGE,"E314")])]});
            var Q6;
            Q6=makeQuery(id+"F1.opExtrude","SWEPT_BODY",BODY,{"disambiguationData":[OSD([sQuery(id+"F0.wireOp",EDGE,"E61.bottom"),sQuery(id+"F0.wireOp",EDGE,"E61.top"),sQuery(id+"F0.wireOp",EDGE,"E61.left"),sQuery(id+"F0.wireOp",EDGE,"E61.right"),sQuery(id+"F0.wireOp",EDGE,"E63.bottom"),sQuery(id+"F0.wireOp",EDGE,"E63.top"),sQuery(id+"F0.wireOp",EDGE,"E63.left"),sQuery(id+"F0.wireOp",EDGE,"E63.right"),sQuery(id+"F0.wireOp",EDGE,"E186"),sQuery(id+"F0.wireOp",EDGE,"E188"),sQuery(id+"F0.wireOp",EDGE,"E190"),sQuery(id+"F0.wireOp",EDGE,"E191"),sQuery(id+"F0.wireOp",EDGE,"E192"),sQuery(id+"F0.wireOp",EDGE,"E193"),sQuery(id+"F0.wireOp",EDGE,"E194"),sQuery(id+"F0.wireOp",EDGE,"E195"),sQuery(id+"F0.wireOp",EDGE,"E197"),sQuery(id+"F0.wireOp",EDGE,"E198"),sQuery(id+"F0.wireOp",EDGE,"E199"),sQuery(id+"F0.wireOp",EDGE,"E200"),sQuery(id+"F0.wireOp",EDGE,"E201")])]});
            var Q7;
            Q7=makeQuery(id+"F1.opExtrude","SWEPT_BODY",BODY,{"disambiguationData":[OSD([sQuery(id+"F0.wireOp",EDGE,"E60.bottom"),sQuery(id+"F0.wireOp",EDGE,"E60.top"),sQuery(id+"F0.wireOp",EDGE,"E60.left"),sQuery(id+"F0.wireOp",EDGE,"E298"),sQuery(id+"F0.wireOp",EDGE,"E299"),sQuery(id+"F0.wireOp",EDGE,"E300")])]});
            var Q8;
            Q8=makeQuery(id+"F1.opExtrude","SWEPT_BODY",BODY,{"disambiguationData":[OSD([sQuery(id+"F0.wireOp",EDGE,"E58.bottom"),sQuery(id+"F0.wireOp",EDGE,"E58.top"),sQuery(id+"F0.wireOp",EDGE,"E58.right"),sQuery(id+"F0.wireOp",EDGE,"E289"),sQuery(id+"F0.wireOp",EDGE,"E290"),sQuery(id+"F0.wireOp",EDGE,"E291"),sQuery(id+"F0.wireOp",EDGE,"E292"),sQuery(id+"F0.wireOp",EDGE,"E293"),sQuery(id+"F0.wireOp",EDGE,"E294")])]});
            var Q9;
            Q9=makeQuery(id+"F1.opExtrude","SWEPT_BODY",BODY,{"disambiguationData":[OSD([sQuery(id+"F0.wireOp",EDGE,"E56.bottom"),sQuery(id+"F0.wireOp",EDGE,"E56.top"),sQuery(id+"F0.wireOp",EDGE,"E56.left"),sQuery(id+"F0.wireOp",EDGE,"E56.right"),sQuery(id+"F0.wireOp",EDGE,"E301"),sQuery(id+"F0.wireOp",EDGE,"E302"),sQuery(id+"F0.wireOp",EDGE,"E303"),sQuery(id+"F0.wireOp",EDGE,"E304"),sQuery(id+"F0.wireOp",EDGE,"E305"),sQuery(id+"F0.wireOp",EDGE,"E306")])]});
            var Q10;
            Q10=makeQuery(id+"F1.opExtrude","SWEPT_BODY",BODY,{"disambiguationData":[OSD([sQuery(id+"F0.wireOp",EDGE,"E55.bottom"),sQuery(id+"F0.wireOp",EDGE,"E55.top"),sQuery(id+"F0.wireOp",EDGE,"E55.left"),sQuery(id+"F0.wireOp",EDGE,"E55.right"),sQuery(id+"F0.wireOp",EDGE,"E59.bottom"),sQuery(id+"F0.wireOp",EDGE,"E59.top"),sQuery(id+"F0.wireOp",EDGE,"E59.left"),sQuery(id+"F0.wireOp",EDGE,"E59.right"),sQuery(id+"F0.wireOp",EDGE,"E178"),sQuery(id+"F0.wireOp",EDGE,"E179"),sQuery(id+"F0.wireOp",EDGE,"E180"),sQuery(id+"F0.wireOp",EDGE,"E182"),sQuery(id+"F0.wireOp",EDGE,"E183"),sQuery(id+"F0.wireOp",EDGE,"E184")])]});
            var Q11;
            Q11=makeQuery(id+"F1.opExtrude","SWEPT_BODY",BODY,{"disambiguationData":[OSD([sQuery(id+"F0.wireOp",EDGE,"E54.bottom"),sQuery(id+"F0.wireOp",EDGE,"E54.top"),sQuery(id+"F0.wireOp",EDGE,"E54.left"),sQuery(id+"F0.wireOp",EDGE,"E54.right"),sQuery(id+"F0.wireOp",EDGE,"E343"),sQuery(id+"F0.wireOp",EDGE,"E344"),sQuery(id+"F0.wireOp",EDGE,"E345")])]});
            var Q12;
            Q12=makeQuery(id+"F1.opExtrude","SWEPT_BODY",BODY,{"disambiguationData":[OSD([sQuery(id+"F0.wireOp",EDGE,"E52.bottom"),sQuery(id+"F0.wireOp",EDGE,"E52.top"),sQuery(id+"F0.wireOp",EDGE,"E52.left"),sQuery(id+"F0.wireOp",EDGE,"E52.right"),sQuery(id+"F0.wireOp",EDGE,"E308"),sQuery(id+"F0.wireOp",EDGE,"E309"),sQuery(id+"F0.wireOp",EDGE,"E310")])]});
            var Q13;
            Q13=makeQuery(id+"F1.opExtrude","SWEPT_BODY",BODY,{"disambiguationData":[OSD([sQuery(id+"F0.wireOp",EDGE,"E51.bottom"),sQuery(id+"F0.wireOp",EDGE,"E51.top"),sQuery(id+"F0.wireOp",EDGE,"E51.left"),sQuery(id+"F0.wireOp",EDGE,"E51.right"),sQuery(id+"F0.wireOp",EDGE,"E331"),sQuery(id+"F0.wireOp",EDGE,"E332"),sQuery(id+"F0.wireOp",EDGE,"E333")])]});
            var Q14;
            Q14=makeQuery(id+"F1.opExtrude","SWEPT_BODY",BODY,{"disambiguationData":[OSD([sQuery(id+"F0.wireOp",EDGE,"E50.bottom"),sQuery(id+"F0.wireOp",EDGE,"E50.top"),sQuery(id+"F0.wireOp",EDGE,"E50.left"),sQuery(id+"F0.wireOp",EDGE,"E50.right"),sQuery(id+"F0.wireOp",EDGE,"E67.bottom"),sQuery(id+"F0.wireOp",EDGE,"E67.top"),sQuery(id+"F0.wireOp",EDGE,"E67.left"),sQuery(id+"F0.wireOp",EDGE,"E67.right"),sQuery(id+"F0.wireOp",EDGE,"E149"),sQuery(id+"F0.wireOp",EDGE,"E151"),sQuery(id+"F0.wireOp",EDGE,"E319"),sQuery(id+"F0.wireOp",EDGE,"E320"),sQuery(id+"F0.wireOp",EDGE,"E321")])]});
            var Q15;
            Q15=makeQuery(id+"F1.opExtrude","SWEPT_BODY",BODY,{"disambiguationData":[OSD([sQuery(id+"F0.wireOp",EDGE,"E48.bottom"),sQuery(id+"F0.wireOp",EDGE,"E48.top"),sQuery(id+"F0.wireOp",EDGE,"E48.left"),sQuery(id+"F0.wireOp",EDGE,"E48.right"),sQuery(id+"F0.wireOp",EDGE,"E315"),sQuery(id+"F0.wireOp",EDGE,"E316"),sQuery(id+"F0.wireOp",EDGE,"E317")])]});
            var Q16;
            Q16=makeQuery(id+"F1.opExtrude","SWEPT_BODY",BODY,{"disambiguationData":[OSD([sQuery(id+"F0.wireOp",EDGE,"E47.bottom"),sQuery(id+"F0.wireOp",EDGE,"E47.top"),sQuery(id+"F0.wireOp",EDGE,"E47.left"),sQuery(id+"F0.wireOp",EDGE,"E47.right"),sQuery(id+"F0.wireOp",EDGE,"E278"),sQuery(id+"F0.wireOp",EDGE,"E279"),sQuery(id+"F0.wireOp",EDGE,"E280")])]});
            var Q17;
            Q17=makeQuery(id+"F1.opExtrude","SWEPT_BODY",BODY,{"disambiguationData":[OSD([sQuery(id+"F0.wireOp",EDGE,"E43.bottom"),sQuery(id+"F0.wireOp",EDGE,"E43.top"),sQuery(id+"F0.wireOp",EDGE,"E43.left"),sQuery(id+"F0.wireOp",EDGE,"E43.right"),sQuery(id+"F0.wireOp",EDGE,"E351"),sQuery(id+"F0.wireOp",EDGE,"E352"),sQuery(id+"F0.wireOp",EDGE,"E353")])]});
            var Q18;
            Q18=makeQuery(id+"F1.opExtrude","SWEPT_BODY",BODY,{"disambiguationData":[OSD([sQuery(id+"F0.wireOp",EDGE,"E42.bottom"),sQuery(id+"F0.wireOp",EDGE,"E42.top"),sQuery(id+"F0.wireOp",EDGE,"E42.left"),sQuery(id+"F0.wireOp",EDGE,"E42.right"),sQuery(id+"F0.wireOp",EDGE,"E355"),sQuery(id+"F0.wireOp",EDGE,"E356"),sQuery(id+"F0.wireOp",EDGE,"E357")])]});
            var Q19;
            Q19=makeQuery(id+"F1.opExtrude","SWEPT_BODY",BODY,{"disambiguationData":[OSD([sQuery(id+"F0.wireOp",EDGE,"E41.bottom"),sQuery(id+"F0.wireOp",EDGE,"E41.top"),sQuery(id+"F0.wireOp",EDGE,"E41.left"),sQuery(id+"F0.wireOp",EDGE,"E41.right"),sQuery(id+"F0.wireOp",EDGE,"E359"),sQuery(id+"F0.wireOp",EDGE,"E360"),sQuery(id+"F0.wireOp",EDGE,"E361")])]});
            var Q20;
            Q20=makeQuery(id+"F1.opExtrude","SWEPT_BODY",BODY,{"disambiguationData":[OSD([sQuery(id+"F0.wireOp",EDGE,"E40.bottom"),sQuery(id+"F0.wireOp",EDGE,"E40.top"),sQuery(id+"F0.wireOp",EDGE,"E40.left"),sQuery(id+"F0.wireOp",EDGE,"E44.bottom"),sQuery(id+"F0.wireOp",EDGE,"E44.top"),sQuery(id+"F0.wireOp",EDGE,"E165"),sQuery(id+"F0.wireOp",EDGE,"E166"),sQuery(id+"F0.wireOp",EDGE,"E167"),sQuery(id+"F0.wireOp",EDGE,"E168"),sQuery(id+"F0.wireOp",EDGE,"E169"),sQuery(id+"F0.wireOp",EDGE,"E286"),sQuery(id+"F0.wireOp",EDGE,"E287"),sQuery(id+"F0.wireOp",EDGE,"E288"),sQuery(id+"F0.wireOp",EDGE,"E363"),sQuery(id+"F0.wireOp",EDGE,"E364"),sQuery(id+"F0.wireOp",EDGE,"E365"),sQuery(id+"F0.wireOp",EDGE,"E366"),sQuery(id+"F0.wireOp",EDGE,"E367"),sQuery(id+"F0.wireOp",EDGE,"E368"),sQuery(id+"F0.wireOp",EDGE,"E369"),sQuery(id+"F0.wireOp",EDGE,"E370"),sQuery(id+"F0.wireOp",EDGE,"E371")])]});
            var Q21;
            Q21=makeQuery(id+"F1.opExtrude","SWEPT_BODY",BODY,{"disambiguationData":[OSD([sQuery(id+"F0.wireOp",EDGE,"E39.bottom"),sQuery(id+"F0.wireOp",EDGE,"E39.top"),sQuery(id+"F0.wireOp",EDGE,"E39.left"),sQuery(id+"F0.wireOp",EDGE,"E39.right"),sQuery(id+"F0.wireOp",EDGE,"E46.bottom"),sQuery(id+"F0.wireOp",EDGE,"E46.top"),sQuery(id+"F0.wireOp",EDGE,"E46.left"),sQuery(id+"F0.wireOp",EDGE,"E46.right"),sQuery(id+"F0.wireOp",EDGE,"E53.bottom"),sQuery(id+"F0.wireOp",EDGE,"E53.top"),sQuery(id+"F0.wireOp",EDGE,"E53.left"),sQuery(id+"F0.wireOp",EDGE,"E53.right"),sQuery(id+"F0.wireOp",EDGE,"E153"),sQuery(id+"F0.wireOp",EDGE,"E154"),sQuery(id+"F0.wireOp",EDGE,"E155"),sQuery(id+"F0.wireOp",EDGE,"E156"),sQuery(id+"F0.wireOp",EDGE,"E157"),sQuery(id+"F0.wireOp",EDGE,"E159"),sQuery(id+"F0.wireOp",EDGE,"E160"),sQuery(id+"F0.wireOp",EDGE,"E161"),sQuery(id+"F0.wireOp",EDGE,"E162"),sQuery(id+"F0.wireOp",EDGE,"E163"),sQuery(id+"F0.wireOp",EDGE,"E170"),sQuery(id+"F0.wireOp",EDGE,"E171"),sQuery(id+"F0.wireOp",EDGE,"E172"),sQuery(id+"F0.wireOp",EDGE,"E174"),sQuery(id+"F0.wireOp",EDGE,"E175"),sQuery(id+"F0.wireOp",EDGE,"E176")])]});
            var Q22;
            Q22=makeQuery(id+"F1.opExtrude","SWEPT_BODY",BODY,{"disambiguationData":[OSD([sQuery(id+"F0.wireOp",EDGE,"E38.bottom"),sQuery(id+"F0.wireOp",EDGE,"E38.top"),sQuery(id+"F0.wireOp",EDGE,"E38.left"),sQuery(id+"F0.wireOp",EDGE,"E38.right")])]});
            var Q23;
            Q23=makeQuery(id+"F1.opExtrude","SWEPT_BODY",BODY,{"disambiguationData":[OSD([sQuery(id+"F0.wireOp",EDGE,"E37.bottom"),sQuery(id+"F0.wireOp",EDGE,"E37.top"),sQuery(id+"F0.wireOp",EDGE,"E37.left"),sQuery(id+"F0.wireOp",EDGE,"E37.right"),sQuery(id+"F0.wireOp",EDGE,"E274"),sQuery(id+"F0.wireOp",EDGE,"E275"),sQuery(id+"F0.wireOp",EDGE,"E276")])]});
            var Q24;
            Q24=makeQuery(id+"F1.opExtrude","SWEPT_BODY",BODY,{"disambiguationData":[OSD([sQuery(id+"F0.wireOp",EDGE,"E36.bottom"),sQuery(id+"F0.wireOp",EDGE,"E36.top"),sQuery(id+"F0.wireOp",EDGE,"E36.left"),sQuery(id+"F0.wireOp",EDGE,"E36.right"),sQuery(id+"F0.wireOp",EDGE,"E49.bottom"),sQuery(id+"F0.wireOp",EDGE,"E49.top"),sQuery(id+"F0.wireOp",EDGE,"E49.left"),sQuery(id+"F0.wireOp",EDGE,"E49.right"),sQuery(id+"F0.wireOp",EDGE,"E68.bottom"),sQuery(id+"F0.wireOp",EDGE,"E68.top"),sQuery(id+"F0.wireOp",EDGE,"E68.left"),sQuery(id+"F0.wireOp",EDGE,"E68.right"),sQuery(id+"F0.wireOp",EDGE,"E129"),sQuery(id+"F0.wireOp",EDGE,"E130"),sQuery(id+"F0.wireOp",EDGE,"E131"),sQuery(id+"F0.wireOp",EDGE,"E133"),sQuery(id+"F0.wireOp",EDGE,"E134"),sQuery(id+"F0.wireOp",EDGE,"E135"),sQuery(id+"F0.wireOp",EDGE,"E137"),sQuery(id+"F0.wireOp",EDGE,"E138"),sQuery(id+"F0.wireOp",EDGE,"E139"),sQuery(id+"F0.wireOp",EDGE,"E140"),sQuery(id+"F0.wireOp",EDGE,"E141"),sQuery(id+"F0.wireOp",EDGE,"E143"),sQuery(id+"F0.wireOp",EDGE,"E144"),sQuery(id+"F0.wireOp",EDGE,"E145"),sQuery(id+"F0.wireOp",EDGE,"E146"),sQuery(id+"F0.wireOp",EDGE,"E147")])]});
            var Q25;
            Q25=makeQuery(id+"F1.opExtrude","SWEPT_BODY",BODY,{"disambiguationData":[OSD([sQuery(id+"F0.wireOp",EDGE,"E35.bottom"),sQuery(id+"F0.wireOp",EDGE,"E35.top"),sQuery(id+"F0.wireOp",EDGE,"E35.left"),sQuery(id+"F0.wireOp",EDGE,"E35.right"),sQuery(id+"F0.wireOp",EDGE,"E270"),sQuery(id+"F0.wireOp",EDGE,"E271"),sQuery(id+"F0.wireOp",EDGE,"E272")])]});
            var Q26;
            Q26=makeQuery(id+"F1.opExtrude","SWEPT_BODY",BODY,{"disambiguationData":[OSD([sQuery(id+"F0.wireOp",EDGE,"E33.bottom"),sQuery(id+"F0.wireOp",EDGE,"E33.top"),sQuery(id+"F0.wireOp",EDGE,"E33.left"),sQuery(id+"F0.wireOp",EDGE,"E33.right"),sQuery(id+"F0.wireOp",EDGE,"E266"),sQuery(id+"F0.wireOp",EDGE,"E267"),sQuery(id+"F0.wireOp",EDGE,"E268")])]});
            var Q27;
            Q27=makeQuery(id+"F1.opExtrude","SWEPT_BODY",BODY,{"disambiguationData":[OSD([sQuery(id+"F0.wireOp",EDGE,"E31.bottom"),sQuery(id+"F0.wireOp",EDGE,"E31.top"),sQuery(id+"F0.wireOp",EDGE,"E31.left"),sQuery(id+"F0.wireOp",EDGE,"E31.right"),sQuery(id+"F0.wireOp",EDGE,"E32.bottom"),sQuery(id+"F0.wireOp",EDGE,"E32.top"),sQuery(id+"F0.wireOp",EDGE,"E32.left"),sQuery(id+"F0.wireOp",EDGE,"E32.right"),sQuery(id+"F0.wireOp",EDGE,"E121"),sQuery(id+"F0.wireOp",EDGE,"E123")])]});
            var Q28;
            Q28=makeQuery(id+"F1.opExtrude","SWEPT_BODY",BODY,{"disambiguationData":[OSD([sQuery(id+"F0.wireOp",EDGE,"E30.bottom"),sQuery(id+"F0.wireOp",EDGE,"E30.top"),sQuery(id+"F0.wireOp",EDGE,"E30.left"),sQuery(id+"F0.wireOp",EDGE,"E30.right"),sQuery(id+"F0.wireOp",EDGE,"E262"),sQuery(id+"F0.wireOp",EDGE,"E263"),sQuery(id+"F0.wireOp",EDGE,"E264")])]});
            var Q29;
            Q29=makeQuery(id+"F1.opExtrude","SWEPT_BODY",BODY,{"disambiguationData":[OSD([sQuery(id+"F0.wireOp",EDGE,"E29.bottom"),sQuery(id+"F0.wireOp",EDGE,"E29.top"),sQuery(id+"F0.wireOp",EDGE,"E29.left"),sQuery(id+"F0.wireOp",EDGE,"E29.right"),sQuery(id+"F0.wireOp",EDGE,"E34.bottom"),sQuery(id+"F0.wireOp",EDGE,"E34.top"),sQuery(id+"F0.wireOp",EDGE,"E34.left"),sQuery(id+"F0.wireOp",EDGE,"E34.right"),sQuery(id+"F0.wireOp",EDGE,"E117"),sQuery(id+"F0.wireOp",EDGE,"E119"),sQuery(id+"F0.wireOp",EDGE,"E120")])]});
            var Q30;
            Q30=makeQuery(id+"F1.opExtrude","SWEPT_BODY",BODY,{"disambiguationData":[OSD([sQuery(id+"F0.wireOp",EDGE,"E28.bottom"),sQuery(id+"F0.wireOp",EDGE,"E28.top"),sQuery(id+"F0.wireOp",EDGE,"E28.left"),sQuery(id+"F0.wireOp",EDGE,"E28.right"),sQuery(id+"F0.wireOp",EDGE,"E347"),sQuery(id+"F0.wireOp",EDGE,"E348"),sQuery(id+"F0.wireOp",EDGE,"E349")])]});
            var Q31;
            Q31=makeQuery(id+"F1.opExtrude","SWEPT_BODY",BODY,{"disambiguationData":[OSD([sQuery(id+"F0.wireOp",EDGE,"E26.bottom"),sQuery(id+"F0.wireOp",EDGE,"E26.top"),sQuery(id+"F0.wireOp",EDGE,"E26.left"),sQuery(id+"F0.wireOp",EDGE,"E26.right"),sQuery(id+"F0.wireOp",EDGE,"E254"),sQuery(id+"F0.wireOp",EDGE,"E255"),sQuery(id+"F0.wireOp",EDGE,"E256")])]});
            var Q32;
            Q32=makeQuery(id+"F1.opExtrude","SWEPT_BODY",BODY,{"disambiguationData":[OSD([sQuery(id+"F0.wireOp",EDGE,"E25.bottom"),sQuery(id+"F0.wireOp",EDGE,"E25.top"),sQuery(id+"F0.wireOp",EDGE,"E25.left"),sQuery(id+"F0.wireOp",EDGE,"E25.right"),sQuery(id+"F0.wireOp",EDGE,"E258"),sQuery(id+"F0.wireOp",EDGE,"E259"),sQuery(id+"F0.wireOp",EDGE,"E260")])]});
            var Q33;
            Q33=makeQuery(id+"F1.opExtrude","SWEPT_BODY",BODY,{"disambiguationData":[OSD([sQuery(id+"F0.wireOp",EDGE,"E24.bottom"),sQuery(id+"F0.wireOp",EDGE,"E24.top"),sQuery(id+"F0.wireOp",EDGE,"E24.left"),sQuery(id+"F0.wireOp",EDGE,"E24.right"),sQuery(id+"F0.wireOp",EDGE,"E27.bottom"),sQuery(id+"F0.wireOp",EDGE,"E27.top"),sQuery(id+"F0.wireOp",EDGE,"E27.left"),sQuery(id+"F0.wireOp",EDGE,"E27.right"),sQuery(id+"F0.wireOp",EDGE,"E107"),sQuery(id+"F0.wireOp",EDGE,"E108"),sQuery(id+"F0.wireOp",EDGE,"E109"),sQuery(id+"F0.wireOp",EDGE,"E110"),sQuery(id+"F0.wireOp",EDGE,"E111"),sQuery(id+"F0.wireOp",EDGE,"E112"),sQuery(id+"F0.wireOp",EDGE,"E113"),sQuery(id+"F0.wireOp",EDGE,"E114"),sQuery(id+"F0.wireOp",EDGE,"E115")])]});
            var Q34;
            Q34=makeQuery(id+"F1.opExtrude","SWEPT_BODY",BODY,{"disambiguationData":[OSD([sQuery(id+"F0.wireOp",EDGE,"E23.bottom"),sQuery(id+"F0.wireOp",EDGE,"E23.top"),sQuery(id+"F0.wireOp",EDGE,"E23.left"),sQuery(id+"F0.wireOp",EDGE,"E23.right"),sQuery(id+"F0.wireOp",EDGE,"E106"),sQuery(id+"F0.wireOp",EDGE,"E250"),sQuery(id+"F0.wireOp",EDGE,"E251"),sQuery(id+"F0.wireOp",EDGE,"E252")])]});
            var Q35;
            Q35=makeQuery(id+"F1.opExtrude","SWEPT_BODY",BODY,{"disambiguationData":[OSD([sQuery(id+"F0.wireOp",EDGE,"E19.bottom"),sQuery(id+"F0.wireOp",EDGE,"E19.top"),sQuery(id+"F0.wireOp",EDGE,"E19.left"),sQuery(id+"F0.wireOp",EDGE,"E19.right"),sQuery(id+"F0.wireOp",EDGE,"E22.bottom"),sQuery(id+"F0.wireOp",EDGE,"E22.top"),sQuery(id+"F0.wireOp",EDGE,"E22.left"),sQuery(id+"F0.wireOp",EDGE,"E22.right"),sQuery(id+"F0.wireOp",EDGE,"E73"),sQuery(id+"F0.wireOp",EDGE,"E75")])]});
            var Q36;
            Q36=makeQuery(id+"F1.opExtrude","SWEPT_BODY",BODY,{"disambiguationData":[OSD([sQuery(id+"F0.wireOp",EDGE,"E18.bottom"),sQuery(id+"F0.wireOp",EDGE,"E18.top"),sQuery(id+"F0.wireOp",EDGE,"E18.left"),sQuery(id+"F0.wireOp",EDGE,"E18.right"),sQuery(id+"F0.wireOp",EDGE,"E21.bottom"),sQuery(id+"F0.wireOp",EDGE,"E21.top"),sQuery(id+"F0.wireOp",EDGE,"E21.left"),sQuery(id+"F0.wireOp",EDGE,"E21.right"),sQuery(id+"F0.wireOp",EDGE,"E102"),sQuery(id+"F0.wireOp",EDGE,"E104")])]});
            var Q37;
            Q37=makeQuery(id+"F1.opExtrude","SWEPT_BODY",BODY,{"disambiguationData":[OSD([sQuery(id+"F0.wireOp",EDGE,"E17.bottom"),sQuery(id+"F0.wireOp",EDGE,"E17.top"),sQuery(id+"F0.wireOp",EDGE,"E17.left"),sQuery(id+"F0.wireOp",EDGE,"E17.right")])]});
            var Q38;
            Q38=makeQuery(id+"F1.opExtrude","SWEPT_BODY",BODY,{"disambiguationData":[OSD([sQuery(id+"F0.wireOp",EDGE,"E16.bottom"),sQuery(id+"F0.wireOp",EDGE,"E16.top"),sQuery(id+"F0.wireOp",EDGE,"E16.left"),sQuery(id+"F0.wireOp",EDGE,"E16.right"),sQuery(id+"F0.wireOp",EDGE,"E237"),sQuery(id+"F0.wireOp",EDGE,"E238"),sQuery(id+"F0.wireOp",EDGE,"E239"),sQuery(id+"F0.wireOp",EDGE,"E240"),sQuery(id+"F0.wireOp",EDGE,"E241")])]});
            var Q39;
            Q39=makeQuery(id+"F1.opExtrude","SWEPT_BODY",BODY,{"disambiguationData":[OSD([sQuery(id+"F0.wireOp",EDGE,"E14.bottom"),sQuery(id+"F0.wireOp",EDGE,"E14.top"),sQuery(id+"F0.wireOp",EDGE,"E14.left"),sQuery(id+"F0.wireOp",EDGE,"E14.right"),sQuery(id+"F0.wireOp",EDGE,"E15.bottom"),sQuery(id+"F0.wireOp",EDGE,"E15.top"),sQuery(id+"F0.wireOp",EDGE,"E15.left"),sQuery(id+"F0.wireOp",EDGE,"E15.right"),sQuery(id+"F0.wireOp",EDGE,"E20.bottom"),sQuery(id+"F0.wireOp",EDGE,"E20.top"),sQuery(id+"F0.wireOp",EDGE,"E20.left"),sQuery(id+"F0.wireOp",EDGE,"E20.right"),sQuery(id+"F0.wireOp",EDGE,"E77"),sQuery(id+"F0.wireOp",EDGE,"E78"),sQuery(id+"F0.wireOp",EDGE,"E79"),sQuery(id+"F0.wireOp",EDGE,"E80"),sQuery(id+"F0.wireOp",EDGE,"E82"),sQuery(id+"F0.wireOp",EDGE,"E83"),sQuery(id+"F0.wireOp",EDGE,"E84"),sQuery(id+"F0.wireOp",EDGE,"E85"),sQuery(id+"F0.wireOp",EDGE,"E87"),sQuery(id+"F0.wireOp",EDGE,"E88"),sQuery(id+"F0.wireOp",EDGE,"E89"),sQuery(id+"F0.wireOp",EDGE,"E90"),sQuery(id+"F0.wireOp",EDGE,"E91")])]});
            var Q40;
            Q40=makeQuery(id+"F1.opExtrude","SWEPT_BODY",BODY,{"disambiguationData":[OSD([sQuery(id+"F0.wireOp",EDGE,"E13.bottom"),sQuery(id+"F0.wireOp",EDGE,"E13.top"),sQuery(id+"F0.wireOp",EDGE,"E13.left"),sQuery(id+"F0.wireOp",EDGE,"E13.right"),sQuery(id+"F0.wireOp",EDGE,"E246"),sQuery(id+"F0.wireOp",EDGE,"E247"),sQuery(id+"F0.wireOp",EDGE,"E248")])]});
            var Q41;
            Q41=makeQuery(id+"F1.opExtrude","SWEPT_BODY",BODY,{"disambiguationData":[OSD([sQuery(id+"F0.wireOp",EDGE,"E12.bottom"),sQuery(id+"F0.wireOp",EDGE,"E12.top"),sQuery(id+"F0.wireOp",EDGE,"E12.left"),sQuery(id+"F0.wireOp",EDGE,"E12.right"),sQuery(id+"F0.wireOp",EDGE,"E125"),sQuery(id+"F0.wireOp",EDGE,"E126"),sQuery(id+"F0.wireOp",EDGE,"E127"),sQuery(id+"F0.wireOp",EDGE,"E242"),sQuery(id+"F0.wireOp",EDGE,"E243"),sQuery(id+"F0.wireOp",EDGE,"E244")])]});
            var Q42;
            Q42=makeQuery(id+"F1.opExtrude","SWEPT_BODY",BODY,{"disambiguationData":[OSD([sQuery(id+"F0.wireOp",EDGE,"E11.bottom"),sQuery(id+"F0.wireOp",EDGE,"E11.top"),sQuery(id+"F0.wireOp",EDGE,"E11.left"),sQuery(id+"F0.wireOp",EDGE,"E11.right"),sQuery(id+"F0.wireOp",EDGE,"E212"),sQuery(id+"F0.wireOp",EDGE,"E213"),sQuery(id+"F0.wireOp",EDGE,"E214")])]});
            var Q43;
            Q43=makeQuery(id+"F1.opExtrude","SWEPT_BODY",BODY,{"disambiguationData":[OSD([sQuery(id+"F0.wireOp",EDGE,"E10.bottom"),sQuery(id+"F0.wireOp",EDGE,"E10.top"),sQuery(id+"F0.wireOp",EDGE,"E10.left"),sQuery(id+"F0.wireOp",EDGE,"E10.right")])]});
            var Q44;
            Q44=makeQuery(id+"F1.opExtrude","SWEPT_BODY",BODY,{"disambiguationData":[OSD([sQuery(id+"F0.wireOp",EDGE,"E9.bottom"),sQuery(id+"F0.wireOp",EDGE,"E9.top"),sQuery(id+"F0.wireOp",EDGE,"E9.left"),sQuery(id+"F0.wireOp",EDGE,"E9.right"),sQuery(id+"F0.wireOp",EDGE,"E216"),sQuery(id+"F0.wireOp",EDGE,"E217"),sQuery(id+"F0.wireOp",EDGE,"E218")])]});
            var Q45;
            Q45=makeQuery(id+"F1.opExtrude","SWEPT_BODY",BODY,{"disambiguationData":[OSD([sQuery(id+"F0.wireOp",EDGE,"E8.bottom"),sQuery(id+"F0.wireOp",EDGE,"E8.top"),sQuery(id+"F0.wireOp",EDGE,"E8.left"),sQuery(id+"F0.wireOp",EDGE,"E8.right"),sQuery(id+"F0.wireOp",EDGE,"E230"),sQuery(id+"F0.wireOp",EDGE,"E231"),sQuery(id+"F0.wireOp",EDGE,"E232")])]});
            var Q46;
            Q46=makeQuery(id+"F1.opExtrude","SWEPT_BODY",BODY,{"disambiguationData":[OSD([sQuery(id+"F0.wireOp",EDGE,"E7.bottom"),sQuery(id+"F0.wireOp",EDGE,"E7.top"),sQuery(id+"F0.wireOp",EDGE,"E7.left"),sQuery(id+"F0.wireOp",EDGE,"E7.right"),sQuery(id+"F0.wireOp",EDGE,"E227"),sQuery(id+"F0.wireOp",EDGE,"E228"),sQuery(id+"F0.wireOp",EDGE,"E229")])]});
            var Q47;
            Q47=makeQuery(id+"F1.opExtrude","SWEPT_BODY",BODY,{"disambiguationData":[OSD([sQuery(id+"F0.wireOp",EDGE,"E6.bottom"),sQuery(id+"F0.wireOp",EDGE,"E6.top"),sQuery(id+"F0.wireOp",EDGE,"E6.left"),sQuery(id+"F0.wireOp",EDGE,"E6.right"),sQuery(id+"F0.wireOp",EDGE,"E221"),sQuery(id+"F0.wireOp",EDGE,"E222"),sQuery(id+"F0.wireOp",EDGE,"E223")])]});
            var Q48;
            Q48=makeQuery(id+"F1.opExtrude","SWEPT_BODY",BODY,{"disambiguationData":[OSD([sQuery(id+"F0.wireOp",EDGE,"E5.bottom"),sQuery(id+"F0.wireOp",EDGE,"E5.top"),sQuery(id+"F0.wireOp",EDGE,"E5.left"),sQuery(id+"F0.wireOp",EDGE,"E5.right"),sQuery(id+"F0.wireOp",EDGE,"E224"),sQuery(id+"F0.wireOp",EDGE,"E225"),sQuery(id+"F0.wireOp",EDGE,"E226")])]});
            var Q49;
            Q49=makeQuery(id+"F1.opExtrude","SWEPT_BODY",BODY,{"disambiguationData":[OSD([sQuery(id+"F0.wireOp",EDGE,"E4.bottom"),sQuery(id+"F0.wireOp",EDGE,"E4.top"),sQuery(id+"F0.wireOp",EDGE,"E4.left"),sQuery(id+"F0.wireOp",EDGE,"E4.right"),sQuery(id+"F0.wireOp",EDGE,"E204"),sQuery(id+"F0.wireOp",EDGE,"E205"),sQuery(id+"F0.wireOp",EDGE,"E206")])]});
            var Q50;
            Q50=makeQuery(id+"F1.opExtrude","SWEPT_BODY",BODY,{"disambiguationData":[OSD([sQuery(id+"F0.wireOp",EDGE,"E3.bottom"),sQuery(id+"F0.wireOp",EDGE,"E3.top"),sQuery(id+"F0.wireOp",EDGE,"E3.left"),sQuery(id+"F0.wireOp",EDGE,"E3.right"),sQuery(id+"F0.wireOp",EDGE,"E208"),sQuery(id+"F0.wireOp",EDGE,"E209"),sQuery(id+"F0.wireOp",EDGE,"E210")])]});
            var Q51;
            Q51=makeQuery(id+"F1.opExtrude","SWEPT_BODY",BODY,{"disambiguationData":[OSD([sQuery(id+"F0.wireOp",EDGE,"E2.bottom"),sQuery(id+"F0.wireOp",EDGE,"E2.top"),sQuery(id+"F0.wireOp",EDGE,"E2.left"),sQuery(id+"F0.wireOp",EDGE,"E2.right"),sQuery(id+"F0.wireOp",EDGE,"E335"),sQuery(id+"F0.wireOp",EDGE,"E336"),sQuery(id+"F0.wireOp",EDGE,"E337")])]});
            var Q52;
            Q52=makeQuery(id+"F1.opExtrude","SWEPT_BODY",BODY,{"disambiguationData":[OSD([sQuery(id+"F0.wireOp",EDGE,"E1.bottom"),sQuery(id+"F0.wireOp",EDGE,"E1.top"),sQuery(id+"F0.wireOp",EDGE,"E1.left"),sQuery(id+"F0.wireOp",EDGE,"E1.right"),sQuery(id+"F0.wireOp",EDGE,"E339"),sQuery(id+"F0.wireOp",EDGE,"E340"),sQuery(id+"F0.wireOp",EDGE,"E341")])]});
            var Q53;
            Q53=makeQuery(id+"F1.opExtrude","SWEPT_BODY",BODY,{"disambiguationData":[OSD([sQuery(id+"F0.wireOp",EDGE,"E57.bottom"),sQuery(id+"F0.wireOp",EDGE,"E57.top"),sQuery(id+"F0.wireOp",EDGE,"E57.right"),sQuery(id+"F0.wireOp",EDGE,"E295"),sQuery(id+"F0.wireOp",EDGE,"E296"),sQuery(id+"F0.wireOp",EDGE,"E297")])]});
            var Q54;
            Q54=makeQuery(id+"F1.opExtrude","SWEPT_BODY",BODY,{"disambiguationData":[OSD([sQuery(id+"F0.wireOp",EDGE,"E45.bottom"),sQuery(id+"F0.wireOp",EDGE,"E45.top"),sQuery(id+"F0.wireOp",EDGE,"E45.left"),sQuery(id+"F0.wireOp",EDGE,"E45.right"),sQuery(id+"F0.wireOp",EDGE,"E282"),sQuery(id+"F0.wireOp",EDGE,"E283"),sQuery(id+"F0.wireOp",EDGE,"E284")])]});
            booleanBodies(context, id + "F2", {"operationType" : BooleanOperationType.UNION, "tools" : qUnion([Q0, Q1, Q2, Q3, Q4, Q5, Q6, Q7, Q8, Q9, Q10, Q11, Q12, Q13, Q14, Q15, Q16, Q17, Q18, Q19, Q20, Q21, Q22, Q23, Q24, Q25, Q26, Q27, Q28, Q29, Q30, Q31, Q32, Q33, Q34, Q35, Q36, Q37, Q38, Q39, Q40, Q41, Q42, Q43, Q44, Q45, Q46, Q47, Q48, Q49, Q50, Q51, Q52, Q53, Q54])});
        }
    });
